FCSTD DOCUMENT  (FreeCAD 0.21R33771 (Git))
Label: RING0_clean
License: All rights reserved
LicenseURL: http://en.wikipedia.org/wiki/All_rights_reserved
objects: Part::Part2DObjectPython×336, App::FeaturePython×48, App::DocumentObjectGroup×2
note: 336 computed .brp shape members not serialized (recipe doc carries the construction recipe); baked Part::Feature solids carry a one-line shape summary decoded from their .brp

FEATURE [Part::Part2DObjectPython] Rectangle  # Draft 2D object (typed FeaturePython)
  Area = 0
  ChamferSize = 0
  Columns = 1
  FilletRadius = 0
  Height = 6
  Length = 6
  MakeFace = false
  Placement = pos=(269.11,-49.15,0) rot=(0,0,1;0rad)
  Rows = 1
FEATURE [App::FeaturePython] Text  # WARN: FeaturePython — macro-defined, semantics opaque (R4)
  Placement = pos=(270.79,-53.3517,0) rot=(0,0,-1;4.73892rad)
  Text = 0
FEATURE [App::FeaturePython] Text001  # WARN: FeaturePython — macro-defined, semantics opaque (R4)
  Placement = pos=(268.047,49.5386,0) rot=(0,0,1;2.6241rad)
  Text = 6.
FEATURE [Part::Part2DObjectPython] Circle  # Draft 2D object (typed FeaturePython)
  Area = 1.13097
  FirstAngle = 0
  LastAngle = 0
  MakeFace = true
  Placement = pos=(275.71,-46.15,0) rot=(0,0,1;0rad)
  Radius = 0.6
FEATURE [Part::Part2DObjectPython] Rectangle001  # Draft 2D object (typed FeaturePython)
  Area = 0
  ChamferSize = 0
  Columns = 1
  FilletRadius = 0
  Height = 6
  Length = 6
  MakeFace = false
  Placement = pos=(271.27,-33.85,0) rot=(0,0,1;0rad)
  Rows = 1
FEATURE [Part::Part2DObjectPython] Circle001  # Draft 2D object (typed FeaturePython)
  Area = 1.13097
  FirstAngle = 0
  LastAngle = 0
  MakeFace = true
  Placement = pos=(277.87,-30.85,0) rot=(0,0,1;0rad)
  Radius = 0.6
FEATURE [Part::Part2DObjectPython] Rectangle002  # Draft 2D object (typed FeaturePython)
  Area = 0
  ChamferSize = 0
  Columns = 1
  FilletRadius = 0
  Height = 6
  Length = 6
  MakeFace = false
  Placement = pos=(279.554,-16.9094,0) rot=(0,0,1;2.00503rad)
  Rows = 1
FEATURE [Part::Part2DObjectPython] Circle002  # Draft 2D object (typed FeaturePython)
  Area = 1.13097
  FirstAngle = 0
  LastAngle = 0
  MakeFace = true
  Placement = pos=(274.055,-12.1841,0) rot=(0,0,1;2.00503rad)
  Radius = 0.6
FEATURE [Part::Part2DObjectPython] Rectangle003  # Draft 2D object (typed FeaturePython)
  Area = 0
  ChamferSize = 0
  Columns = 1
  FilletRadius = 0
  Height = 6
  Length = 6
  MakeFace = false
  Placement = pos=(279.954,-1.537,0) rot=(0,0,1;1.98549rad)
  Rows = 1
FEATURE [Part::Part2DObjectPython] Circle003  # Draft 2D object (typed FeaturePython)
  Area = 1.13097
  FirstAngle = 0
  LastAngle = 0
  MakeFace = true
  Placement = pos=(274.55,3.29487,0) rot=(0,0,1;1.98549rad)
  Radius = 0.6
FEATURE [Part::Part2DObjectPython] Rectangle004  # Draft 2D object (typed FeaturePython)
  Area = 0
  ChamferSize = 0
  Columns = 1
  FilletRadius = 0
  Height = 6
  Length = 6
  MakeFace = false
  Placement = pos=(279.425,13.6792,0) rot=(0,0,1;1.92562rad)
  Rows = 1
FEATURE [Part::Part2DObjectPython] Circle004  # Draft 2D object (typed FeaturePython)
  Area = 1.13097
  FirstAngle = 0
  LastAngle = 0
  MakeFace = true
  Placement = pos=(274.319,18.8257,0) rot=(0,0,1;1.92562rad)
  Radius = 0.6
FEATURE [Part::Part2DObjectPython] Rectangle005  # Draft 2D object (typed FeaturePython)
  Area = 0
  ChamferSize = 0
  Columns = 1
  FilletRadius = 0
  Height = 6
  Length = 6
  MakeFace = false
  Placement = pos=(277.955,28.7473,0) rot=(0,0,1;1.83766rad)
  Rows = 1
FEATURE [Part::Part2DObjectPython] Circle005  # Draft 2D object (typed FeaturePython)
  Area = 1.13097
  FirstAngle = 0
  LastAngle = 0
  MakeFace = true
  Placement = pos=(273.321,34.3226,0) rot=(0,0,1;1.83766rad)
  Radius = 0.6
FEATURE [Part::Part2DObjectPython] Rectangle006  # Draft 2D object (typed FeaturePython)
  Area = 0
  ChamferSize = 0
  Columns = 1
  FilletRadius = 0
  Height = 6
  Length = 6
  MakeFace = false
  Placement = pos=(275.609,43.7506,0) rot=(0,0,1;1.7551rad)
  Rows = 1
FEATURE [Part::Part2DObjectPython] Circle006  # Draft 2D object (typed FeaturePython)
  Area = 1.13097
  FirstAngle = 0
  LastAngle = 0
  MakeFace = true
  Placement = pos=(271.45,49.689,0) rot=(0,0,1;1.7551rad)
  Radius = 0.6
FEATURE [Part::Part2DObjectPython] Rectangle007  # Draft 2D object (typed FeaturePython)
  Area = 0
  ChamferSize = 0
  Columns = 1
  FilletRadius = 0
  Height = 6
  Length = 6
  MakeFace = false
  Placement = pos=(262.426,94.0073,0) rot=(0,0,1;1.84307rad)
  Rows = 1
FEATURE [App::FeaturePython] Text002  # WARN: FeaturePython — macro-defined, semantics opaque (R4)
  Placement = pos=(261.188,89.1931,0) rot=(0,0,-1;4.21532rad)
  Text = 0
FEATURE [App::FeaturePython] Text003  # WARN: FeaturePython — macro-defined, semantics opaque (R4)
  Placement = pos=(207.363,176.926,0) rot=(0,0,1;3.1477rad)
  Text = 7
FEATURE [Part::Part2DObjectPython] Circle007  # Draft 2D object (typed FeaturePython)
  Area = 1.13097
  FirstAngle = 0
  LastAngle = 0
  MakeFace = true
  Placement = pos=(257.762,99.5574,0) rot=(0,0,1;1.84307rad)
  Radius = 0.6
FEATURE [Part::Part2DObjectPython] Rectangle008  # Draft 2D object (typed FeaturePython)
  Area = 0
  ChamferSize = 0
  Columns = 1
  FilletRadius = 0
  Height = 6
  Length = 6
  MakeFace = false
  Placement = pos=(257.005,109.172,0) rot=(0,0,1;2.05774rad)
  Rows = 1
FEATURE [Part::Part2DObjectPython] Circle008  # Draft 2D object (typed FeaturePython)
  Area = 1.13097
  FirstAngle = 0
  LastAngle = 0
  MakeFace = true
  Placement = pos=(251.265,113.602,0) rot=(0,0,1;2.05774rad)
  Radius = 0.6
FEATURE [Part::Part2DObjectPython] Rectangle009  # Draft 2D object (typed FeaturePython)
  Area = 0
  ChamferSize = 0
  Columns = 1
  FilletRadius = 0
  Height = 6
  Length = 6
  MakeFace = false
  Placement = pos=(250.401,125.732,0) rot=(0,0,1;2.67315rad)
  Rows = 1
FEATURE [Part::Part2DObjectPython] Circle009  # Draft 2D object (typed FeaturePython)
  Area = 1.13097
  FirstAngle = 0
  LastAngle = 0
  MakeFace = true
  Placement = pos=(243.158,126.035,0) rot=(0,0,1;2.67315rad)
  Radius = 0.6
FEATURE [Part::Part2DObjectPython] Rectangle010  # Draft 2D object (typed FeaturePython)
  Area = 0
  ChamferSize = 0
  Columns = 1
  FilletRadius = 0
  Height = 6
  Length = 6
  MakeFace = false
  Placement = pos=(237.816,142.068,0) rot=(0,0,-1;2.06856rad)
  Rows = 1
FEATURE [Part::Part2DObjectPython] Circle010  # Draft 2D object (typed FeaturePython)
  Area = 1.13097
  FirstAngle = 0
  LastAngle = 0
  MakeFace = true
  Placement = pos=(237.301,134.837,0) rot=(0,0,-1;2.06856rad)
  Radius = 0.6
FEATURE [Part::Part2DObjectPython] Rectangle011  # Draft 2D object (typed FeaturePython)
  Area = 0
  ChamferSize = 0
  Columns = 1
  FilletRadius = 0
  Height = 6
  Length = 6
  MakeFace = false
  Placement = pos=(227.695,153.917,0) rot=(0,0,-1;1.49278rad)
  Rows = 1
FEATURE [Part::Part2DObjectPython] Circle011  # Draft 2D object (typed FeaturePython)
  Area = 1.13097
  FirstAngle = 0
  LastAngle = 0
  MakeFace = true
  Placement = pos=(231.201,147.571,0) rot=(0,0,-1;1.49278rad)
  Radius = 0.6
FEATURE [Part::Part2DObjectPython] Rectangle012  # Draft 2D object (typed FeaturePython)
  Area = 0
  ChamferSize = 0
  Columns = 1
  FilletRadius = 0
  Height = 6
  Length = 6
  MakeFace = false
  Placement = pos=(218.268,165.67,0) rot=(0,0,-1;1.22889rad)
  Rows = 1
FEATURE [Part::Part2DObjectPython] Circle012  # Draft 2D object (typed FeaturePython)
  Area = 1.13097
  FirstAngle = 0
  LastAngle = 0
  MakeFace = true
  Placement = pos=(223.307,160.458,0) rot=(0,0,-1;1.22889rad)
  Radius = 0.6
FEATURE [Part::Part2DObjectPython] Rectangle013  # Draft 2D object (typed FeaturePython)
  Area = 0
  ChamferSize = 0
  Columns = 1
  FilletRadius = 0
  Height = 6
  Length = 6
  MakeFace = false
  Placement = pos=(208.466,177.056,0) rot=(0,0,-1;1.03219rad)
  Rows = 1
FEATURE [Part::Part2DObjectPython] Circle013  # Draft 2D object (typed FeaturePython)
  Area = 1.13097
  FirstAngle = 0
  LastAngle = 0
  MakeFace = true
  Placement = pos=(214.427,172.93,0) rot=(0,0,-1;1.03219rad)
  Radius = 0.6
FEATURE [Part::Part2DObjectPython] Rectangle014  # Draft 2D object (typed FeaturePython)
  Area = 0
  ChamferSize = 0
  Columns = 1
  FilletRadius = 0
  Height = 6
  Length = 6
  MakeFace = false
  Placement = pos=(171.985,211.268,0) rot=(0,0,-1;0.47089rad)
  Rows = 1
FEATURE [App::FeaturePython] Text004  # WARN: FeaturePython — macro-defined, semantics opaque (R4)
  Placement = pos=(181.597,207.836,0) rot=(0,0,-1;3.69172rad)
  Text = 0
FEATURE [App::FeaturePython] Text005  # WARN: FeaturePython — macro-defined, semantics opaque (R4)
  Placement = pos=(91.1209,256.902,0) rot=(0,0,1;3.6713rad)
  Text = 8
FEATURE [Part::Part2DObjectPython] Circle014  # Draft 2D object (typed FeaturePython)
  Area = 1.13097
  FirstAngle = 0
  LastAngle = 0
  MakeFace = true
  Placement = pos=(179.228,210.947,0) rot=(0,0,-1;0.47089rad)
  Radius = 0.6
FEATURE [Part::Part2DObjectPython] Rectangle015  # Draft 2D object (typed FeaturePython)
  Area = 0
  ChamferSize = 0
  Columns = 1
  FilletRadius = 0
  Height = 6
  Length = 6
  MakeFace = false
  Placement = pos=(160.075,220.163,0) rot=(0,0,-1;0.311367rad)
  Rows = 1
FEATURE [Part::Part2DObjectPython] Circle015  # Draft 2D object (typed FeaturePython)
  Area = 1.13097
  FirstAngle = 0
  LastAngle = 0
  MakeFace = true
  Placement = pos=(167.277,220.997,0) rot=(0,0,-1;0.311367rad)
  Radius = 0.6
FEATURE [Part::Part2DObjectPython] Rectangle016  # Draft 2D object (typed FeaturePython)
  Area = 0
  ChamferSize = 0
  Columns = 1
  FilletRadius = 0
  Height = 6
  Length = 6
  MakeFace = false
  Placement = pos=(147.739,228.41,0) rot=(0,0,-1;0.152367rad)
  Rows = 1
FEATURE [Part::Part2DObjectPython] Circle016  # Draft 2D object (typed FeaturePython)
  Area = 1.13097
  FirstAngle = 0
  LastAngle = 0
  MakeFace = true
  Placement = pos=(154.718,230.374,0) rot=(0,0,-1;0.152367rad)
  Radius = 0.6
FEATURE [Part::Part2DObjectPython] Rectangle017  # Draft 2D object (typed FeaturePython)
  Area = 0
  ChamferSize = 0
  Columns = 1
  FilletRadius = 0
  Height = 6
  Length = 6
  MakeFace = false
  Placement = pos=(134.999,236.021,0) rot=(0,0,-1;0.000349rad)
  Rows = 1
FEATURE [Part::Part2DObjectPython] Circle017  # Draft 2D object (typed FeaturePython)
  Area = 1.13097
  FirstAngle = 0
  LastAngle = 0
  MakeFace = true
  Placement = pos=(141.6,239.019,0) rot=(0,0,-1;0.000349rad)
  Radius = 0.6
FEATURE [Part::Part2DObjectPython] Rectangle018  # Draft 2D object (typed FeaturePython)
  Area = 0
  ChamferSize = 0
  Columns = 1
  FilletRadius = 0
  Height = 6
  Length = 6
  MakeFace = false
  Placement = pos=(121.98,242.893,0) rot=(0,0,1;0.175406rad)
  Rows = 1
FEATURE [Part::Part2DObjectPython] Circle018  # Draft 2D object (typed FeaturePython)
  Area = 1.13097
  FirstAngle = 0
  LastAngle = 0
  MakeFace = true
  Placement = pos=(127.955,246.998,0) rot=(0,0,1;0.175406rad)
  Radius = 0.6
FEATURE [Part::Part2DObjectPython] Rectangle019  # Draft 2D object (typed FeaturePython)
  Area = 0
  ChamferSize = 0
  Columns = 1
  FilletRadius = 0
  Height = 6
  Length = 6
  MakeFace = false
  Placement = pos=(107.42,249.95,0) rot=(0,0,1;0rad)
  Rows = 1
FEATURE [Part::Part2DObjectPython] Circle019  # Draft 2D object (typed FeaturePython)
  Area = 1.13097
  FirstAngle = 0
  LastAngle = 0
  MakeFace = true
  Placement = pos=(114.02,252.95,0) rot=(0,0,1;0rad)
  Radius = 0.6
FEATURE [Part::Part2DObjectPython] Rectangle020  # Draft 2D object (typed FeaturePython)
  Area = 0
  ChamferSize = 0
  Columns = 1
  FilletRadius = 0
  Height = 6
  Length = 6
  MakeFace = false
  Placement = pos=(93.09,255.73,0) rot=(0,0,1;0rad)
  Rows = 1
FEATURE [Part::Part2DObjectPython] Circle020  # Draft 2D object (typed FeaturePython)
  Area = 1.13097
  FirstAngle = 0
  LastAngle = 0
  MakeFace = true
  Placement = pos=(99.69,258.73,0) rot=(0,0,1;0rad)
  Radius = 0.6
FEATURE [Part::Part2DObjectPython] Rectangle021  # Draft 2D object (typed FeaturePython)
  Area = 0
  ChamferSize = 0
  Columns = 1
  FilletRadius = 0
  Height = 6
  Length = 6
  MakeFace = false
  Placement = pos=(43.15,269.11,0) rot=(0,0,1;0rad)
  Rows = 1
FEATURE [App::FeaturePython] Text006  # WARN: FeaturePython — macro-defined, semantics opaque (R4)
  Placement = pos=(53.3517,270.79,0) rot=(0,0,-1;3.16812rad)
  Text = 0
FEATURE [App::FeaturePython] Text007  # WARN: FeaturePython — macro-defined, semantics opaque (R4)
  Placement = pos=(-49.5386,268.047,0) rot=(0,0,1;4.1949rad)
  Text = 9
FEATURE [Part::Part2DObjectPython] Circle021  # Draft 2D object (typed FeaturePython)
  Area = 1.13097
  FirstAngle = 0
  LastAngle = 0
  MakeFace = true
  Placement = pos=(49.75,272.11,0) rot=(0,0,1;0rad)
  Radius = 0.6
FEATURE [Part::Part2DObjectPython] Rectangle022  # Draft 2D object (typed FeaturePython)
  Area = 0
  ChamferSize = 0
  Columns = 1
  FilletRadius = 0
  Height = 6
  Length = 6
  MakeFace = false
  Placement = pos=(27.85,271.27,0) rot=(0,0,1;0rad)
  Rows = 1
FEATURE [Part::Part2DObjectPython] Circle022  # Draft 2D object (typed FeaturePython)
  Area = 1.13097
  FirstAngle = 0
  LastAngle = 0
  MakeFace = true
  Placement = pos=(34.45,274.27,0) rot=(0,0,1;0rad)
  Radius = 0.6
FEATURE [Part::Part2DObjectPython] Rectangle023  # Draft 2D object (typed FeaturePython)
  Area = 0
  ChamferSize = 0
  Columns = 1
  FilletRadius = 0
  Height = 6
  Length = 6
  MakeFace = false
  Placement = pos=(12.45,272.57,0) rot=(0,0,1;0rad)
  Rows = 1
FEATURE [Part::Part2DObjectPython] Circle023  # Draft 2D object (typed FeaturePython)
  Area = 1.13097
  FirstAngle = 0
  LastAngle = 0
  MakeFace = true
  Placement = pos=(19.05,275.57,0) rot=(0,0,1;0rad)
  Radius = 0.6
FEATURE [Part::Part2DObjectPython] Rectangle024  # Draft 2D object (typed FeaturePython)
  Area = 0
  ChamferSize = 0
  Columns = 1
  FilletRadius = 0
  Height = 6
  Length = 6
  MakeFace = false
  Placement = pos=(-3,273,0) rot=(0,0,1;0rad)
  Rows = 1
FEATURE [Part::Part2DObjectPython] Circle024  # Draft 2D object (typed FeaturePython)
  Area = 1.13097
  FirstAngle = 0
  LastAngle = 0
  MakeFace = true
  Placement = pos=(3.6,276,0) rot=(0,0,1;0rad)
  Radius = 0.6
FEATURE [Part::Part2DObjectPython] Rectangle025  # Draft 2D object (typed FeaturePython)
  Area = 0
  ChamferSize = 0
  Columns = 1
  FilletRadius = 0
  Height = 6
  Length = 6
  MakeFace = false
  Placement = pos=(-11.2074,275.547,0) rot=(0,0,1;2.35078rad)
  Rows = 1
FEATURE [Part::Part2DObjectPython] Circle025  # Draft 2D object (typed FeaturePython)
  Area = 1.13097
  FirstAngle = 0
  LastAngle = 0
  MakeFace = true
  Placement = pos=(-17.9818,278.129,0) rot=(0,0,1;2.35078rad)
  Radius = 0.6
FEATURE [Part::Part2DObjectPython] Rectangle026  # Draft 2D object (typed FeaturePython)
  Area = 0
  ChamferSize = 0
  Columns = 1
  FilletRadius = 0
  Height = 6
  Length = 6
  MakeFace = false
  Placement = pos=(-26.6143,274.513,0) rot=(0,0,1;2.41344rad)
  Rows = 1
FEATURE [Part::Part2DObjectPython] Circle026  # Draft 2D object (typed FeaturePython)
  Area = 1.13097
  FirstAngle = 0
  LastAngle = 0
  MakeFace = true
  Placement = pos=(-33.5371,276.666,0) rot=(0,0,1;2.41344rad)
  Radius = 0.6
FEATURE [Part::Part2DObjectPython] Rectangle027  # Draft 2D object (typed FeaturePython)
  Area = 0
  ChamferSize = 0
  Columns = 1
  FilletRadius = 0
  Height = 6
  Length = 6
  MakeFace = false
  Placement = pos=(-41.9327,272.573,0) rot=(0,0,1;2.46545rad)
  Rows = 1
FEATURE [Part::Part2DObjectPython] Circle027  # Draft 2D object (typed FeaturePython)
  Area = 1.13097
  FirstAngle = 0
  LastAngle = 0
  MakeFace = true
  Placement = pos=(-48.958,274.363,0) rot=(0,0,1;2.46545rad)
  Radius = 0.6
FEATURE [Part::Part2DObjectPython] Rectangle028  # Draft 2D object (typed FeaturePython)
  Area = 0
  ChamferSize = 0
  Columns = 1
  FilletRadius = 0
  Height = 6
  Length = 6
  MakeFace = false
  Placement = pos=(-92.1068,260.191,0) rot=(0,0,1;2.7077rad)
  Rows = 1
FEATURE [App::FeaturePython] Text008  # WARN: FeaturePython — macro-defined, semantics opaque (R4)
  Placement = pos=(-89.1931,261.188,0) rot=(0,0,-1;2.64452rad)
  Text = 0
FEATURE [App::FeaturePython] Text009  # WARN: FeaturePython — macro-defined, semantics opaque (R4)
  Placement = pos=(-176.926,207.363,0) rot=(0,0,1;4.7185rad)
  Text = 10
FEATURE [Part::Part2DObjectPython] Circle028  # Draft 2D object (typed FeaturePython)
  Area = 1.13097
  FirstAngle = 0
  LastAngle = 0
  MakeFace = true
  Placement = pos=(-99.3564,260.243,0) rot=(0,0,1;2.7077rad)
  Radius = 0.6
FEATURE [Part::Part2DObjectPython] Rectangle029  # Draft 2D object (typed FeaturePython)
  Area = 0
  ChamferSize = 0
  Columns = 1
  FilletRadius = 0
  Height = 6
  Length = 6
  MakeFace = false
  Placement = pos=(-106.607,254.81,0) rot=(0,0,1;2.80998rad)
  Rows = 1
FEATURE [Part::Part2DObjectPython] Circle029  # Draft 2D object (typed FeaturePython)
  Area = 1.13097
  FirstAngle = 0
  LastAngle = 0
  MakeFace = true
  Placement = pos=(-113.824,254.122,0) rot=(0,0,1;2.80998rad)
  Radius = 0.6
FEATURE [Part::Part2DObjectPython] Rectangle030  # Draft 2D object (typed FeaturePython)
  Area = 0
  ChamferSize = 0
  Columns = 1
  FilletRadius = 0
  Height = 6
  Length = 6
  MakeFace = false
  Placement = pos=(-120.843,248.666,0) rot=(0,0,1;2.92814rad)
  Rows = 1
FEATURE [Part::Part2DObjectPython] Circle030  # Draft 2D object (typed FeaturePython)
  Area = 1.13097
  FirstAngle = 0
  LastAngle = 0
  MakeFace = true
  Placement = pos=(-127.928,247.133,0) rot=(0,0,1;2.92814rad)
  Radius = 0.6
FEATURE [Part::Part2DObjectPython] Rectangle031  # Draft 2D object (typed FeaturePython)
  Area = 0
  ChamferSize = 0
  Columns = 1
  FilletRadius = 0
  Height = 6
  Length = 6
  MakeFace = false
  Placement = pos=(-134.775,241.777,0) rot=(0,0,1;3.06358rad)
  Rows = 1
FEATURE [Part::Part2DObjectPython] Circle031  # Draft 2D object (typed FeaturePython)
  Area = 1.13097
  FirstAngle = 0
  LastAngle = 0
  MakeFace = true
  Placement = pos=(-141.589,239.301,0) rot=(0,0,1;3.06358rad)
  Radius = 0.6
FEATURE [Part::Part2DObjectPython] Rectangle032  # Draft 2D object (typed FeaturePython)
  Area = 0
  ChamferSize = 0
  Columns = 1
  FilletRadius = 0
  Height = 6
  Length = 6
  MakeFace = false
  Placement = pos=(-148.392,234.135,0) rot=(0,0,1;3.21612rad)
  Rows = 1
FEATURE [Part::Part2DObjectPython] Circle032  # Draft 2D object (typed FeaturePython)
  Area = 1.13097
  FirstAngle = 0
  LastAngle = 0
  MakeFace = true
  Placement = pos=(-154.75,230.652,0) rot=(0,0,1;3.21612rad)
  Radius = 0.6
FEATURE [Part::Part2DObjectPython] Rectangle033  # Draft 2D object (typed FeaturePython)
  Area = 0
  ChamferSize = 0
  Columns = 1
  FilletRadius = 0
  Height = 6
  Length = 6
  MakeFace = false
  Placement = pos=(-161.674,225.742,0) rot=(0,0,1;3.38838rad)
  Rows = 1
FEATURE [Part::Part2DObjectPython] Circle033  # Draft 2D object (typed FeaturePython)
  Area = 1.13097
  FirstAngle = 0
  LastAngle = 0
  MakeFace = true
  Placement = pos=(-167.341,221.221,0) rot=(0,0,1;3.38838rad)
  Radius = 0.6
FEATURE [Part::Part2DObjectPython] Rectangle034  # Draft 2D object (typed FeaturePython)
  Area = 0
  ChamferSize = 0
  Columns = 1
  FilletRadius = 0
  Height = 6
  Length = 6
  MakeFace = false
  Placement = pos=(-174.591,216.575,0) rot=(0,0,1;3.58351rad)
  Rows = 1
FEATURE [Part::Part2DObjectPython] Circle034  # Draft 2D object (typed FeaturePython)
  Area = 1.13097
  FirstAngle = 0
  LastAngle = 0
  MakeFace = true
  Placement = pos=(-179.274,211.04,0) rot=(0,0,1;3.58351rad)
  Radius = 0.6
FEATURE [Part::Part2DObjectPython] Rectangle035  # Draft 2D object (typed FeaturePython)
  Area = 0
  ChamferSize = 0
  Columns = 1
  FilletRadius = 0
  Height = 6
  Length = 6
  MakeFace = false
  Placement = pos=(-215.58,173.02,0) rot=(0,0,1;0rad)
  Rows = 1
FEATURE [App::FeaturePython] Text010  # WARN: FeaturePython — macro-defined, semantics opaque (R4)
  Placement = pos=(-207.836,181.597,0) rot=(0,0,-1;2.12092rad)
  Text = 0
FEATURE [App::FeaturePython] Text011  # WARN: FeaturePython — macro-defined, semantics opaque (R4)
  Placement = pos=(-256.902,91.1209,0) rot=(0,0,1;5.2421rad)
  Text = 11
FEATURE [Part::Part2DObjectPython] Circle035  # Draft 2D object (typed FeaturePython)
  Area = 1.13097
  FirstAngle = 0
  LastAngle = 0
  MakeFace = true
  Placement = pos=(-208.98,176.02,0) rot=(0,0,1;0rad)
  Radius = 0.6
FEATURE [Part::Part2DObjectPython] Rectangle036  # Draft 2D object (typed FeaturePython)
  Area = 0
  ChamferSize = 0
  Columns = 1
  FilletRadius = 0
  Height = 6
  Length = 6
  MakeFace = false
  Placement = pos=(-225.1,160.85,0) rot=(0,0,1;0rad)
  Rows = 1
FEATURE [Part::Part2DObjectPython] Circle036  # Draft 2D object (typed FeaturePython)
  Area = 1.13097
  FirstAngle = 0
  LastAngle = 0
  MakeFace = true
  Placement = pos=(-218.5,163.85,0) rot=(0,0,1;0rad)
  Radius = 0.6
FEATURE [Part::Part2DObjectPython] Rectangle037  # Draft 2D object (typed FeaturePython)
  Area = 0
  ChamferSize = 0
  Columns = 1
  FilletRadius = 0
  Height = 6
  Length = 6
  MakeFace = false
  Placement = pos=(-235.027,152.225,0) rot=(0,0,-1;1.03917rad)
  Rows = 1
FEATURE [Part::Part2DObjectPython] Circle037  # Draft 2D object (typed FeaturePython)
  Area = 1.13097
  FirstAngle = 0
  LastAngle = 0
  MakeFace = true
  Placement = pos=(-229.095,148.057,0) rot=(0,0,-1;1.03917rad)
  Radius = 0.6
FEATURE [Part::Part2DObjectPython] Rectangle038  # Draft 2D object (typed FeaturePython)
  Area = 0
  ChamferSize = 0
  Columns = 1
  FilletRadius = 0
  Height = 6
  Length = 6
  MakeFace = false
  Placement = pos=(-243.205,137.304,0) rot=(0,0,-1;0.620639rad)
  Rows = 1
FEATURE [Part::Part2DObjectPython] Circle038  # Draft 2D object (typed FeaturePython)
  Area = 1.13097
  FirstAngle = 0
  LastAngle = 0
  MakeFace = true
  Placement = pos=(-236.091,135.906,0) rot=(0,0,-1;0.620639rad)
  Radius = 0.6
FEATURE [Part::Part2DObjectPython] Rectangle039  # Draft 2D object (typed FeaturePython)
  Area = 0
  ChamferSize = 0
  Columns = 1
  FilletRadius = 0
  Height = 6
  Length = 6
  MakeFace = false
  Placement = pos=(-249.949,122.131,0) rot=(0,0,-1;0.218341rad)
  Rows = 1
FEATURE [Part::Part2DObjectPython] Circle039  # Draft 2D object (typed FeaturePython)
  Area = 1.13097
  FirstAngle = 0
  LastAngle = 0
  MakeFace = true
  Placement = pos=(-242.855,123.63,0) rot=(0,0,-1;0.218341rad)
  Radius = 0.6
FEATURE [Part::Part2DObjectPython] Rectangle040  # Draft 2D object (typed FeaturePython)
  Area = 0
  ChamferSize = 0
  Columns = 1
  FilletRadius = 0
  Height = 6
  Length = 6
  MakeFace = false
  Placement = pos=(-255.95,107.42,0) rot=(0,0,1;0rad)
  Rows = 1
FEATURE [Part::Part2DObjectPython] Circle040  # Draft 2D object (typed FeaturePython)
  Area = 1.13097
  FirstAngle = 0
  LastAngle = 0
  MakeFace = true
  Placement = pos=(-249.35,110.42,0) rot=(0,0,1;0rad)
  Radius = 0.6
FEATURE [Part::Part2DObjectPython] Rectangle041  # Draft 2D object (typed FeaturePython)
  Area = 0
  ChamferSize = 0
  Columns = 1
  FilletRadius = 0
  Height = 6
  Length = 6
  MakeFace = false
  Placement = pos=(-261.73,93.09,0) rot=(0,0,1;0rad)
  Rows = 1
FEATURE [Part::Part2DObjectPython] Circle041  # Draft 2D object (typed FeaturePython)
  Area = 1.13097
  FirstAngle = 0
  LastAngle = 0
  MakeFace = true
  Placement = pos=(-255.13,96.09,0) rot=(0,0,1;0rad)
  Radius = 0.6
FEATURE [Part::Part2DObjectPython] Rectangle042  # Draft 2D object (typed FeaturePython)
  Area = 0
  ChamferSize = 0
  Columns = 1
  FilletRadius = 0
  Height = 6
  Length = 6
  MakeFace = false
  Placement = pos=(-275.11,43.15,0) rot=(0,0,1;0rad)
  Rows = 1
FEATURE [App::FeaturePython] Text012  # WARN: FeaturePython — macro-defined, semantics opaque (R4)
  Placement = pos=(-270.79,53.3517,0) rot=(0,0,-1;1.59733rad)
  Text = 0
FEATURE [App::FeaturePython] Text013  # WARN: FeaturePython — macro-defined, semantics opaque (R4)
  Placement = pos=(-268.047,-49.5386,0) rot=(0,0,1;5.7657rad)
  Text = 12
FEATURE [Part::Part2DObjectPython] Circle042  # Draft 2D object (typed FeaturePython)
  Area = 1.13097
  FirstAngle = 0
  LastAngle = 0
  MakeFace = true
  Placement = pos=(-268.51,46.15,0) rot=(0,0,1;0rad)
  Radius = 0.6
FEATURE [Part::Part2DObjectPython] Rectangle043  # Draft 2D object (typed FeaturePython)
  Area = 0
  ChamferSize = 0
  Columns = 1
  FilletRadius = 0
  Height = 6
  Length = 6
  MakeFace = false
  Placement = pos=(-277.27,27.85,0) rot=(0,0,1;0rad)
  Rows = 1
FEATURE [Part::Part2DObjectPython] Circle043  # Draft 2D object (typed FeaturePython)
  Area = 1.13097
  FirstAngle = 0
  LastAngle = 0
  MakeFace = true
  Placement = pos=(-270.67,30.85,0) rot=(0,0,1;0rad)
  Radius = 0.6
FEATURE [Part::Part2DObjectPython] Rectangle044  # Draft 2D object (typed FeaturePython)
  Area = 0
  ChamferSize = 0
  Columns = 1
  FilletRadius = 0
  Height = 6
  Length = 6
  MakeFace = false
  Placement = pos=(-278.57,12.45,0) rot=(0,0,1;0rad)
  Rows = 1
FEATURE [Part::Part2DObjectPython] Circle044  # Draft 2D object (typed FeaturePython)
  Area = 1.13097
  FirstAngle = 0
  LastAngle = 0
  MakeFace = true
  Placement = pos=(-271.97,15.45,0) rot=(0,0,1;0rad)
  Radius = 0.6
FEATURE [Part::Part2DObjectPython] Rectangle045  # Draft 2D object (typed FeaturePython)
  Area = 0
  ChamferSize = 0
  Columns = 1
  FilletRadius = 0
  Height = 6
  Length = 6
  MakeFace = false
  Placement = pos=(-272.368,-2.19273,0) rot=(0,0,1;1.81305rad)
  Rows = 1
FEATURE [Part::Part2DObjectPython] Circle045  # Draft 2D object (typed FeaturePython)
  Area = 1.13097
  FirstAngle = 0
  LastAngle = 0
  MakeFace = true
  Placement = pos=(-276.864,3.49488,0) rot=(0,0,1;1.81305rad)
  Radius = 0.6
FEATURE [Part::Part2DObjectPython] Rectangle046  # Draft 2D object (typed FeaturePython)
  Area = 0
  ChamferSize = 0
  Columns = 1
  FilletRadius = 0
  Height = 6
  Length = 6
  MakeFace = false
  Placement = pos=(-271.699,-17.1865,0) rot=(0,0,1;1.93452rad)
  Rows = 1
FEATURE [Part::Part2DObjectPython] Circle046  # Draft 2D object (typed FeaturePython)
  Area = 1.13097
  FirstAngle = 0
  LastAngle = 0
  MakeFace = true
  Placement = pos=(-276.851,-12.0855,0) rot=(0,0,1;1.93452rad)
  Radius = 0.6
FEATURE [Part::Part2DObjectPython] Rectangle047  # Draft 2D object (typed FeaturePython)
  Area = 0
  ChamferSize = 0
  Columns = 1
  FilletRadius = 0
  Height = 6
  Length = 6
  MakeFace = false
  Placement = pos=(-270.258,-32.2306,0) rot=(0,0,1;2.02476rad)
  Rows = 1
FEATURE [Part::Part2DObjectPython] Circle047  # Draft 2D object (typed FeaturePython)
  Area = 1.13097
  FirstAngle = 0
  LastAngle = 0
  MakeFace = true
  Placement = pos=(-275.849,-27.6146,0) rot=(0,0,1;2.02476rad)
  Radius = 0.6
FEATURE [Part::Part2DObjectPython] Rectangle048  # Draft 2D object (typed FeaturePython)
  Area = 0
  ChamferSize = 0
  Columns = 1
  FilletRadius = 0
  Height = 6
  Length = 6
  MakeFace = false
  Placement = pos=(-268.022,-47.2859,0) rot=(0,0,1;2.08514rad)
  Rows = 1
FEATURE [Part::Part2DObjectPython] Circle048  # Draft 2D object (typed FeaturePython)
  Area = 1.13097
  FirstAngle = 0
  LastAngle = 0
  MakeFace = true
  Placement = pos=(-273.881,-43.0158,0) rot=(0,0,1;2.08514rad)
  Radius = 0.6
FEATURE [Part::Part2DObjectPython] Rectangle049  # Draft 2D object (typed FeaturePython)
  Area = 0
  ChamferSize = 0
  Columns = 1
  FilletRadius = 0
  Height = 6
  Length = 6
  MakeFace = false
  Placement = pos=(-254.646,-97.2388,0) rot=(0,0,1;2.082rad)
  Rows = 1
FEATURE [App::FeaturePython] Text014  # WARN: FeaturePython — macro-defined, semantics opaque (R4)
  Placement = pos=(-261.188,-89.1931,0) rot=(0,0,-1;1.07373rad)
  Text = 0
FEATURE [App::FeaturePython] Text015  # WARN: FeaturePython — macro-defined, semantics opaque (R4)
  Placement = pos=(-207.363,-176.926,0) rot=(0,0,-1;6.27708rad)
  Text = 1
FEATURE [Part::Part2DObjectPython] Circle049  # Draft 2D object (typed FeaturePython)
  Area = 1.13097
  FirstAngle = 0
  LastAngle = 0
  MakeFace = true
  Placement = pos=(-260.491,-92.9502,0) rot=(0,0,1;2.082rad)
  Radius = 0.6
FEATURE [Part::Part2DObjectPython] Rectangle050  # Draft 2D object (typed FeaturePython)
  Area = 0
  ChamferSize = 0
  Columns = 1
  FilletRadius = 0
  Height = 6
  Length = 6
  MakeFace = false
  Placement = pos=(-248.887,-111.641,0) rot=(0,0,1;2.06438rad)
  Rows = 1
FEATURE [Part::Part2DObjectPython] Circle050  # Draft 2D object (typed FeaturePython)
  Area = 1.13097
  FirstAngle = 0
  LastAngle = 0
  MakeFace = true
  Placement = pos=(-254.656,-107.25,0) rot=(0,0,1;2.06438rad)
  Radius = 0.6
FEATURE [Part::Part2DObjectPython] Rectangle051  # Draft 2D object (typed FeaturePython)
  Area = 0
  ChamferSize = 0
  Columns = 1
  FilletRadius = 0
  Height = 6
  Length = 6
  MakeFace = false
  Placement = pos=(-242.318,-125.667,0) rot=(0,0,1;2.05547rad)
  Rows = 1
FEATURE [Part::Part2DObjectPython] Circle051  # Draft 2D object (typed FeaturePython)
  Area = 1.13097
  FirstAngle = 0
  LastAngle = 0
  MakeFace = true
  Placement = pos=(-248.047,-121.225,0) rot=(0,0,1;2.05547rad)
  Radius = 0.6
FEATURE [Part::Part2DObjectPython] Rectangle052  # Draft 2D object (typed FeaturePython)
  Area = 0
  ChamferSize = 0
  Columns = 1
  FilletRadius = 0
  Height = 6
  Length = 6
  MakeFace = false
  Placement = pos=(-235.006,-139.374,0) rot=(0,0,1;2.0265rad)
  Rows = 1
FEATURE [Part::Part2DObjectPython] Circle052  # Draft 2D object (typed FeaturePython)
  Area = 1.13097
  FirstAngle = 0
  LastAngle = 0
  MakeFace = true
  Placement = pos=(-240.604,-134.767,0) rot=(0,0,1;2.0265rad)
  Radius = 0.6
FEATURE [Part::Part2DObjectPython] Rectangle053  # Draft 2D object (typed FeaturePython)
  Area = 0
  ChamferSize = 0
  Columns = 1
  FilletRadius = 0
  Height = 6
  Length = 6
  MakeFace = false
  Placement = pos=(-229.308,-155.084,0) rot=(0,0,1;1.17513rad)
  Rows = 1
FEATURE [Part::Part2DObjectPython] Circle053  # Draft 2D object (typed FeaturePython)
  Area = 1.13097
  FirstAngle = 0
  LastAngle = 0
  MakeFace = true
  Placement = pos=(-229.532,-147.838,0) rot=(0,0,1;1.17513rad)
  Radius = 0.6
FEATURE [Part::Part2DObjectPython] Rectangle054  # Draft 2D object (typed FeaturePython)
  Area = 0
  ChamferSize = 0
  Columns = 1
  FilletRadius = 0
  Height = 6
  Length = 6
  MakeFace = false
  Placement = pos=(-225.094,-166.856,0) rot=(0,0,1;0.00192rad)
  Rows = 1
FEATURE [Part::Part2DObjectPython] Circle054  # Draft 2D object (typed FeaturePython)
  Area = 1.13097
  FirstAngle = 0
  LastAngle = 0
  MakeFace = true
  Placement = pos=(-218.5,-163.843,0) rot=(0,0,1;0.00192rad)
  Radius = 0.6
FEATURE [Part::Part2DObjectPython] Rectangle055  # Draft 2D object (typed FeaturePython)
  Area = 0
  ChamferSize = 0
  Columns = 1
  FilletRadius = 0
  Height = 6
  Length = 6
  MakeFace = false
  Placement = pos=(-215.58,-179.02,0) rot=(0,0,1;0rad)
  Rows = 1
FEATURE [Part::Part2DObjectPython] Circle055  # Draft 2D object (typed FeaturePython)
  Area = 1.13097
  FirstAngle = 0
  LastAngle = 0
  MakeFace = true
  Placement = pos=(-208.98,-176.02,0) rot=(0,0,1;0rad)
  Radius = 0.6
FEATURE [Part::Part2DObjectPython] Rectangle056  # Draft 2D object (typed FeaturePython)
  Area = 0
  ChamferSize = 0
  Columns = 1
  FilletRadius = 0
  Height = 6
  Length = 6
  MakeFace = false
  Placement = pos=(-179.02,-215.58,0) rot=(0,0,1;0rad)
  Rows = 1
FEATURE [App::FeaturePython] Text016  # WARN: FeaturePython — macro-defined, semantics opaque (R4)
  Placement = pos=(-181.597,-207.836,0) rot=(0,0,-1;0.550128rad)
  Text = 0
FEATURE [App::FeaturePython] Text017  # WARN: FeaturePython — macro-defined, semantics opaque (R4)
  Placement = pos=(-91.1209,-256.902,0) rot=(0,0,-1;5.75348rad)
  Text = 2
FEATURE [Part::Part2DObjectPython] Circle056  # Draft 2D object (typed FeaturePython)
  Area = 1.13097
  FirstAngle = 0
  LastAngle = 0
  MakeFace = true
  Placement = pos=(-172.42,-212.58,0) rot=(0,0,1;0rad)
  Radius = 0.6
FEATURE [Part::Part2DObjectPython] Rectangle057  # Draft 2D object (typed FeaturePython)
  Area = 0
  ChamferSize = 0
  Columns = 1
  FilletRadius = 0
  Height = 6
  Length = 6
  MakeFace = false
  Placement = pos=(-166.85,-225.1,0) rot=(0,0,1;0rad)
  Rows = 1
FEATURE [Part::Part2DObjectPython] Circle057  # Draft 2D object (typed FeaturePython)
  Area = 1.13097
  FirstAngle = 0
  LastAngle = 0
  MakeFace = true
  Placement = pos=(-160.25,-222.1,0) rot=(0,0,1;0rad)
  Radius = 0.6
FEATURE [Part::Part2DObjectPython] Rectangle058  # Draft 2D object (typed FeaturePython)
  Area = 0
  ChamferSize = 0
  Columns = 1
  FilletRadius = 0
  Height = 6
  Length = 6
  MakeFace = false
  Placement = pos=(-153.761,-234.272,0) rot=(0,0,1;0.125489rad)
  Rows = 1
FEATURE [Part::Part2DObjectPython] Circle058  # Draft 2D object (typed FeaturePython)
  Area = 1.13097
  FirstAngle = 0
  LastAngle = 0
  MakeFace = true
  Placement = pos=(-147.588,-230.469,0) rot=(0,0,1;0.125489rad)
  Radius = 0.6
FEATURE [Part::Part2DObjectPython] Rectangle059  # Draft 2D object (typed FeaturePython)
  Area = 0
  ChamferSize = 0
  Columns = 1
  FilletRadius = 0
  Height = 6
  Length = 6
  MakeFace = false
  Placement = pos=(-140.093,-242.71,0) rot=(0,0,1;0.269479rad)
  Rows = 1
FEATURE [Part::Part2DObjectPython] Circle059  # Draft 2D object (typed FeaturePython)
  Area = 1.13097
  FirstAngle = 0
  LastAngle = 0
  MakeFace = true
  Placement = pos=(-134.53,-238.062,0) rot=(0,0,1;0.269479rad)
  Radius = 0.6
FEATURE [Part::Part2DObjectPython] Rectangle060  # Draft 2D object (typed FeaturePython)
  Area = 0
  ChamferSize = 0
  Columns = 1
  FilletRadius = 0
  Height = 6
  Length = 6
  MakeFace = false
  Placement = pos=(-125.95,-250.323,0) rot=(0,0,1;0.413818rad)
  Rows = 1
FEATURE [Part::Part2DObjectPython] Circle060  # Draft 2D object (typed FeaturePython)
  Area = 1.13097
  FirstAngle = 0
  LastAngle = 0
  MakeFace = true
  Placement = pos=(-121.114,-244.922,0) rot=(0,0,1;0.413818rad)
  Radius = 0.6
FEATURE [Part::Part2DObjectPython] Rectangle061  # Draft 2D object (typed FeaturePython)
  Area = 0
  ChamferSize = 0
  Columns = 1
  FilletRadius = 0
  Height = 6
  Length = 6
  MakeFace = false
  Placement = pos=(-111.377,-257.083,0) rot=(0,0,1;0.557982rad)
  Rows = 1
FEATURE [Part::Part2DObjectPython] Circle061  # Draft 2D object (typed FeaturePython)
  Area = 1.13097
  FirstAngle = 0
  LastAngle = 0
  MakeFace = true
  Placement = pos=(-107.366,-251.044,0) rot=(0,0,1;0.557982rad)
  Radius = 0.6
FEATURE [Part::Part2DObjectPython] Rectangle062  # Draft 2D object (typed FeaturePython)
  Area = 0
  ChamferSize = 0
  Columns = 1
  FilletRadius = 0
  Height = 6
  Length = 6
  MakeFace = false
  Placement = pos=(-96.445,-262.958,0) rot=(0,0,1;0.701622rad)
  Rows = 1
FEATURE [Part::Part2DObjectPython] Circle062  # Draft 2D object (typed FeaturePython)
  Area = 1.13097
  FirstAngle = 0
  LastAngle = 0
  MakeFace = true
  Placement = pos=(-93.3403,-256.406,0) rot=(0,0,1;0.701622rad)
  Radius = 0.6
FEATURE [Part::Part2DObjectPython] Rectangle063  # Draft 2D object (typed FeaturePython)
  Area = 0
  ChamferSize = 0
  Columns = 1
  FilletRadius = 0
  Height = 6
  Length = 6
  MakeFace = false
  Placement = pos=(-44.495,-276.017,0) rot=(0,0,1;1.18613rad)
  Rows = 1
FEATURE [App::FeaturePython] Text018  # WARN: FeaturePython — macro-defined, semantics opaque (R4)
  Placement = pos=(-53.3517,-270.79,0) rot=(0,0,1;6.25666rad)
  Text = 0
FEATURE [App::FeaturePython] Text019  # WARN: FeaturePython — macro-defined, semantics opaque (R4)
  Placement = pos=(49.5386,-268.047,0) rot=(0,0,1;1.05331rad)
  Text = 3
FEATURE [Part::Part2DObjectPython] Circle063  # Draft 2D object (typed FeaturePython)
  Area = 1.13097
  FirstAngle = 0
  LastAngle = 0
  MakeFace = true
  Placement = pos=(-44.7991,-268.773,0) rot=(0,0,1;1.18613rad)
  Radius = 0.6
FEATURE [Part::Part2DObjectPython] Rectangle064  # Draft 2D object (typed FeaturePython)
  Area = 0
  ChamferSize = 0
  Columns = 1
  FilletRadius = 0
  Height = 6
  Length = 6
  MakeFace = false
  Placement = pos=(-28.6459,-277.895,0) rot=(0,0,1;1.33169rad)
  Rows = 1
FEATURE [Part::Part2DObjectPython] Circle064  # Draft 2D object (typed FeaturePython)
  Area = 1.13097
  FirstAngle = 0
  LastAngle = 0
  MakeFace = true
  Placement = pos=(-29.9974,-270.772,0) rot=(0,0,1;1.33169rad)
  Radius = 0.6
FEATURE [Part::Part2DObjectPython] Rectangle065  # Draft 2D object (typed FeaturePython)
  Area = 0
  ChamferSize = 0
  Columns = 1
  FilletRadius = 0
  Height = 6
  Length = 6
  MakeFace = false
  Placement = pos=(-18.45,-278.57,0) rot=(0,0,1;0rad)
  Rows = 1
FEATURE [Part::Part2DObjectPython] Circle065  # Draft 2D object (typed FeaturePython)
  Area = 1.13097
  FirstAngle = 0
  LastAngle = 0
  MakeFace = true
  Placement = pos=(-11.85,-275.57,0) rot=(0,0,1;0rad)
  Radius = 0.6
FEATURE [Part::Part2DObjectPython] Rectangle066  # Draft 2D object (typed FeaturePython)
  Area = 0
  ChamferSize = 0
  Columns = 1
  FilletRadius = 0
  Height = 6
  Length = 6
  MakeFace = false
  Placement = pos=(3.1687,-278.821,0) rot=(0,0,1;1.62874rad)
  Rows = 1
FEATURE [Part::Part2DObjectPython] Circle066  # Draft 2D object (typed FeaturePython)
  Area = 1.13097
  FirstAngle = 0
  LastAngle = 0
  MakeFace = true
  Placement = pos=(-0.208485,-272.406,0) rot=(0,0,1;1.62874rad)
  Radius = 0.6
FEATURE [Part::Part2DObjectPython] Rectangle067  # Draft 2D object (typed FeaturePython)
  Area = 0
  ChamferSize = 0
  Columns = 1
  FilletRadius = 0
  Height = 6
  Length = 6
  MakeFace = false
  Placement = pos=(19.0033,-277.888,0) rot=(0,0,1;1.77814rad)
  Rows = 1
FEATURE [Part::Part2DObjectPython] Circle067  # Draft 2D object (typed FeaturePython)
  Area = 1.13097
  FirstAngle = 0
  LastAngle = 0
  MakeFace = true
  Placement = pos=(14.7089,-272.047,0) rot=(0,0,1;1.77814rad)
  Radius = 0.6
FEATURE [Part::Part2DObjectPython] Rectangle068  # Draft 2D object (typed FeaturePython)
  Area = 0
  ChamferSize = 0
  Columns = 1
  FilletRadius = 0
  Height = 6
  Length = 6
  MakeFace = false
  Placement = pos=(34.7128,-276.025,0) rot=(0,0,1;1.92981rad)
  Rows = 1
FEATURE [Part::Part2DObjectPython] Circle068  # Draft 2D object (typed FeaturePython)
  Area = 1.13097
  FirstAngle = 0
  LastAngle = 0
  MakeFace = true
  Placement = pos=(29.5851,-270.9,0) rot=(0,0,1;1.92981rad)
  Radius = 0.6
FEATURE [Part::Part2DObjectPython] Rectangle069  # Draft 2D object (typed FeaturePython)
  Area = 0
  ChamferSize = 0
  Columns = 1
  FilletRadius = 0
  Height = 6
  Length = 6
  MakeFace = false
  Placement = pos=(50.2362,-273.252,0) rot=(0,0,1;2.08375rad)
  Rows = 1
FEATURE [Part::Part2DObjectPython] Circle069  # Draft 2D object (typed FeaturePython)
  Area = 1.13097
  FirstAngle = 0
  LastAngle = 0
  MakeFace = true
  Placement = pos=(44.3833,-268.973,0) rot=(0,0,1;2.08375rad)
  Radius = 0.6
FEATURE [Part::Part2DObjectPython] Rectangle070  # Draft 2D object (typed FeaturePython)
  Area = 0
  ChamferSize = 0
  Columns = 1
  FilletRadius = 0
  Height = 6
  Length = 6
  MakeFace = false
  Placement = pos=(100.186,-257.625,0) rot=(0,0,1;2.61957rad)
  Rows = 1
FEATURE [App::FeaturePython] Text020  # WARN: FeaturePython — macro-defined, semantics opaque (R4)
  Placement = pos=(89.1931,-261.188,0) rot=(0,0,-1;5.78612rad)
  Text = 0
FEATURE [App::FeaturePython] Text021  # WARN: FeaturePython — macro-defined, semantics opaque (R4)
  Placement = pos=(176.926,-207.363,0) rot=(0,0,1;1.57691rad)
  Text = 4
FEATURE [Part::Part2DObjectPython] Circle070  # Draft 2D object (typed FeaturePython)
  Area = 1.13097
  FirstAngle = 0
  LastAngle = 0
  MakeFace = true
  Placement = pos=(92.9695,-256.935,0) rot=(0,0,1;2.61957rad)
  Radius = 0.6
FEATURE [Part::Part2DObjectPython] Rectangle071  # Draft 2D object (typed FeaturePython)
  Area = 0
  ChamferSize = 0
  Columns = 1
  FilletRadius = 0
  Height = 6
  Length = 6
  MakeFace = false
  Placement = pos=(114.274,-251.175,0) rot=(0,0,1;2.78781rad)
  Rows = 1
FEATURE [Part::Part2DObjectPython] Circle071  # Draft 2D object (typed FeaturePython)
  Area = 1.13097
  FirstAngle = 0
  LastAngle = 0
  MakeFace = true
  Placement = pos=(107.043,-251.703,0) rot=(0,0,1;2.78781rad)
  Radius = 0.6
FEATURE [Part::Part2DObjectPython] Rectangle072  # Draft 2D object (typed FeaturePython)
  Area = 0
  ChamferSize = 0
  Columns = 1
  FilletRadius = 0
  Height = 6
  Length = 6
  MakeFace = false
  Placement = pos=(127.902,-243.961,0) rot=(0,0,1;2.96008rad)
  Rows = 1
FEATURE [Part::Part2DObjectPython] Circle072  # Draft 2D object (typed FeaturePython)
  Area = 1.13097
  FirstAngle = 0
  LastAngle = 0
  MakeFace = true
  Placement = pos=(120.869,-245.72,0) rot=(0,0,1;2.96008rad)
  Radius = 0.6
FEATURE [Part::Part2DObjectPython] Rectangle073  # Draft 2D object (typed FeaturePython)
  Area = 0
  ChamferSize = 0
  Columns = 1
  FilletRadius = 0
  Height = 6
  Length = 6
  MakeFace = false
  Placement = pos=(141.016,-236.036,0) rot=(0,0,1;3.13636rad)
  Rows = 1
FEATURE [Part::Part2DObjectPython] Circle073  # Draft 2D object (typed FeaturePython)
  Area = 1.13097
  FirstAngle = 0
  LastAngle = 0
  MakeFace = true
  Placement = pos=(134.4,-239.001,0) rot=(0,0,1;3.13636rad)
  Radius = 0.6
FEATURE [Part::Part2DObjectPython] Rectangle074  # Draft 2D object (typed FeaturePython)
  Area = 0
  ChamferSize = 0
  Columns = 1
  FilletRadius = 0
  Height = 6
  Length = 6
  MakeFace = false
  Placement = pos=(153.592,-227.443,0) rot=(0,0,1;3.31665rad)
  Rows = 1
FEATURE [Part::Part2DObjectPython] Circle074  # Draft 2D object (typed FeaturePython)
  Area = 1.13097
  FirstAngle = 0
  LastAngle = 0
  MakeFace = true
  Placement = pos=(147.615,-231.547,0) rot=(0,0,1;3.31665rad)
  Radius = 0.6
FEATURE [Part::Part2DObjectPython] Rectangle075  # Draft 2D object (typed FeaturePython)
  Area = 0
  ChamferSize = 0
  Columns = 1
  FilletRadius = 0
  Height = 6
  Length = 6
  MakeFace = false
  Placement = pos=(165.62,-218.244,0) rot=(0,0,1;3.49659rad)
  Rows = 1
FEATURE [Part::Part2DObjectPython] Circle075  # Draft 2D object (typed FeaturePython)
  Area = 1.13097
  FirstAngle = 0
  LastAngle = 0
  MakeFace = true
  Placement = pos=(160.474,-223.351,0) rot=(0,0,1;3.49659rad)
  Radius = 0.6
FEATURE [Part::Part2DObjectPython] Rectangle076  # Draft 2D object (typed FeaturePython)
  Area = 0
  ChamferSize = 0
  Columns = 1
  FilletRadius = 0
  Height = 6
  Length = 6
  MakeFace = false
  Placement = pos=(177.079,-208.472,0) rot=(0,0,1;3.67479rad)
  Rows = 1
FEATURE [Part::Part2DObjectPython] Circle076  # Draft 2D object (typed FeaturePython)
  Area = 1.13097
  FirstAngle = 0
  LastAngle = 0
  MakeFace = true
  Placement = pos=(172.92,-214.41,0) rot=(0,0,1;3.67479rad)
  Radius = 0.6
FEATURE [Part::Part2DObjectPython] Rectangle077  # Draft 2D object (typed FeaturePython)
  Area = 0
  ChamferSize = 0
  Columns = 1
  FilletRadius = 0
  Height = 6
  Length = 6
  MakeFace = false
  Placement = pos=(211.679,-171.874,0) rot=(0,0,1;4.14097rad)
  Rows = 1
FEATURE [App::FeaturePython] Text022  # WARN: FeaturePython — macro-defined, semantics opaque (R4)
  Placement = pos=(207.836,-181.597,0) rot=(0,0,-1;5.26252rad)
  Text = 0
FEATURE [App::FeaturePython] Text023  # WARN: FeaturePython — macro-defined, semantics opaque (R4)
  Placement = pos=(256.902,-91.1209,0) rot=(0,0,1;2.1005rad)
  Text = 5
FEATURE [Part::Part2DObjectPython] Circle077  # Draft 2D object (typed FeaturePython)
  Area = 1.13097
  FirstAngle = 0
  LastAngle = 0
  MakeFace = true
  Placement = pos=(210.633,-179.048,0) rot=(0,0,1;4.14097rad)
  Radius = 0.6
FEATURE [Part::Part2DObjectPython] Rectangle078  # Draft 2D object (typed FeaturePython)
  Area = 0
  ChamferSize = 0
  Columns = 1
  FilletRadius = 0
  Height = 6
  Length = 6
  MakeFace = false
  Placement = pos=(224.524,-160.368,0) rot=(0,0,1;3.31874rad)
  Rows = 1
FEATURE [Part::Part2DObjectPython] Circle078  # Draft 2D object (typed FeaturePython)
  Area = 1.13097
  FirstAngle = 0
  LastAngle = 0
  MakeFace = true
  Placement = pos=(218.556,-164.484,0) rot=(0,0,1;3.31874rad)
  Radius = 0.6
FEATURE [Part::Part2DObjectPython] Rectangle079  # Draft 2D object (typed FeaturePython)
  Area = 0
  ChamferSize = 0
  Columns = 1
  FilletRadius = 0
  Height = 6
  Length = 6
  MakeFace = false
  Placement = pos=(233.417,-154.59,0) rot=(0,0,1;1.41476rad)
  Rows = 1
FEATURE [Part::Part2DObjectPython] Circle079  # Draft 2D object (typed FeaturePython)
  Area = 1.13097
  FirstAngle = 0
  LastAngle = 0
  MakeFace = true
  Placement = pos=(231.479,-147.604,0) rot=(0,0,1;1.41476rad)
  Radius = 0.6
FEATURE [Part::Part2DObjectPython] Rectangle080  # Draft 2D object (typed FeaturePython)
  Area = 0
  ChamferSize = 0
  Columns = 1
  FilletRadius = 0
  Height = 6
  Length = 6
  MakeFace = false
  Placement = pos=(241.673,-141.311,0) rot=(0,0,1;1.46084rad)
  Rows = 1
FEATURE [Part::Part2DObjectPython] Circle080  # Draft 2D object (typed FeaturePython)
  Area = 1.13097
  FirstAngle = 0
  LastAngle = 0
  MakeFace = true
  Placement = pos=(239.415,-134.422,0) rot=(0,0,1;1.46084rad)
  Radius = 0.6
FEATURE [Part::Part2DObjectPython] Rectangle081  # Draft 2D object (typed FeaturePython)
  Area = 0
  ChamferSize = 0
  Columns = 1
  FilletRadius = 0
  Height = 6
  Length = 6
  MakeFace = false
  Placement = pos=(249.26,-127.516,0) rot=(0,0,1;1.53484rad)
  Rows = 1
FEATURE [Part::Part2DObjectPython] Circle081  # Draft 2D object (typed FeaturePython)
  Area = 1.13097
  FirstAngle = 0
  LastAngle = 0
  MakeFace = true
  Placement = pos=(246.499,-120.812,0) rot=(0,0,1;1.53484rad)
  Radius = 0.6
FEATURE [Part::Part2DObjectPython] Rectangle082  # Draft 2D object (typed FeaturePython)
  Area = 0
  ChamferSize = 0
  Columns = 1
  FilletRadius = 0
  Height = 6
  Length = 6
  MakeFace = false
  Placement = pos=(256.074,-113.29,0) rot=(0,0,1;1.61321rad)
  Rows = 1
FEATURE [Part::Part2DObjectPython] Circle082  # Draft 2D object (typed FeaturePython)
  Area = 1.13097
  FirstAngle = 0
  LastAngle = 0
  MakeFace = true
  Placement = pos=(252.797,-106.823,0) rot=(0,0,1;1.61321rad)
  Radius = 0.6
FEATURE [Part::Part2DObjectPython] Rectangle083  # Draft 2D object (typed FeaturePython)
  Area = 0
  ChamferSize = 0
  Columns = 1
  FilletRadius = 0
  Height = 6
  Length = 6
  MakeFace = false
  Placement = pos=(262.079,-98.695,0) rot=(0,0,1;1.69506rad)
  Rows = 1
FEATURE [Part::Part2DObjectPython] Circle083  # Draft 2D object (typed FeaturePython)
  Area = 1.13097
  FirstAngle = 0
  LastAngle = 0
  MakeFace = true
  Placement = pos=(258.284,-92.5178,0) rot=(0,0,1;1.69506rad)
  Radius = 0.6
FEATURE [App::DocumentObjectGroup] Everything
  Group = -> [Rectangle,Circle,Rectangle001,Circle001,Rectangle002,Circle002,Rectangle003,Circle003,Rectangle004,Circle004,Rectangle005,Circle005,Rectangle006,Circle006,Rectangle007,Circle007,Rectangle008,Circle008,Rectangle009,Circle009,Rectangle010,Circle010,Rectangle011,Circle011,Rectangle012,Circle012,Rectangle013,Circle013,Rectangle014,Circle014,Rectangle015,Circle015,Rectangle016,Circle016,Rectangle017,+133 more]
FEATURE [Part::Part2DObjectPython] Rectangle084  # Draft 2D object (typed FeaturePython)
  Area = 0
  ChamferSize = 0
  Columns = 1
  FilletRadius = 0
  Height = 6
  Length = 6
  MakeFace = false
  Placement = pos=(275.479,-48.7292,0) rot=(0,0,1;1.70274rad)
  Rows = 1
FEATURE [App::FeaturePython] Text024  # WARN: FeaturePython — macro-defined, semantics opaque (R4)
  Placement = pos=(270.79,-53.3517,0) rot=(0,0,-1;4.73892rad)
  Text = 0
FEATURE [App::FeaturePython] Text025  # WARN: FeaturePython — macro-defined, semantics opaque (R4)
  Placement = pos=(268.047,49.5386,0) rot=(0,0,1;2.6241rad)
  Text = 6.
FEATURE [Part::Part2DObjectPython] Circle084  # Draft 2D object (typed FeaturePython)
  Area = 1.13097
  FirstAngle = 0
  LastAngle = 0
  MakeFace = true
  Placement = pos=(271.636,-42.5813,0) rot=(0,0,1;1.70274rad)
  Radius = 0.6
FEATURE [Part::Part2DObjectPython] Rectangle085  # Draft 2D object (typed FeaturePython)
  Area = 0
  ChamferSize = 0
  Columns = 1
  FilletRadius = 0
  Height = 6
  Length = 6
  MakeFace = false
  Placement = pos=(277.675,-33.3808,0) rot=(0,0,1;1.71705rad)
  Rows = 1
FEATURE [Part::Part2DObjectPython] Circle085  # Draft 2D object (typed FeaturePython)
  Area = 1.13097
  FirstAngle = 0
  LastAngle = 0
  MakeFace = true
  Placement = pos=(273.745,-27.2884,0) rot=(0,0,1;1.71705rad)
  Radius = 0.6
FEATURE [Part::Part2DObjectPython] Rectangle086  # Draft 2D object (typed FeaturePython)
  Area = 0
  ChamferSize = 0
  Columns = 1
  FilletRadius = 0
  Height = 6
  Length = 6
  MakeFace = false
  Placement = pos=(278.941,-18.0257,0) rot=(0,0,1;1.70379rad)
  Rows = 1
FEATURE [Part::Part2DObjectPython] Circle086  # Draft 2D object (typed FeaturePython)
  Area = 1.13097
  FirstAngle = 0
  LastAngle = 0
  MakeFace = true
  Placement = pos=(275.093,-11.8818,0) rot=(0,0,1;1.70379rad)
  Radius = 0.6
FEATURE [Part::Part2DObjectPython] Rectangle087  # Draft 2D object (typed FeaturePython)
  Area = 0
  ChamferSize = 0
  Columns = 1
  FilletRadius = 0
  Height = 6
  Length = 6
  MakeFace = false
  Placement = pos=(279.274,-2.69808,0) rot=(0,0,1;1.66696rad)
  Rows = 1
FEATURE [Part::Part2DObjectPython] Circle087  # Draft 2D object (typed FeaturePython)
  Area = 1.13097
  FirstAngle = 0
  LastAngle = 0
  MakeFace = true
  Placement = pos=(275.654,3.58337,0) rot=(0,0,1;1.66696rad)
  Radius = 0.6
FEATURE [Part::Part2DObjectPython] Rectangle088  # Draft 2D object (typed FeaturePython)
  Area = 0
  ChamferSize = 0
  Columns = 1
  FilletRadius = 0
  Height = 6
  Length = 6
  MakeFace = false
  Placement = pos=(278.705,12.5914,0) rot=(0,0,1;1.61687rad)
  Rows = 1
FEATURE [Part::Part2DObjectPython] Circle088  # Draft 2D object (typed FeaturePython)
  Area = 1.13097
  FirstAngle = 0
  LastAngle = 0
  MakeFace = true
  Placement = pos=(275.404,19.0462,0) rot=(0,0,1;1.61687rad)
  Radius = 0.6
FEATURE [Part::Part2DObjectPython] Rectangle089  # Draft 2D object (typed FeaturePython)
  Area = 0
  ChamferSize = 0
  Columns = 1
  FilletRadius = 0
  Height = 6
  Length = 6
  MakeFace = false
  Placement = pos=(277.289,27.8694,0) rot=(0,0,1;1.57725rad)
  Rows = 1
FEATURE [Part::Part2DObjectPython] Circle089  # Draft 2D object (typed FeaturePython)
  Area = 1.13097
  FirstAngle = 0
  LastAngle = 0
  MakeFace = true
  Placement = pos=(274.247,34.4499,0) rot=(0,0,1;1.57725rad)
  Radius = 0.6
FEATURE [Part::Part2DObjectPython] Rectangle090  # Draft 2D object (typed FeaturePython)
  Area = 0
  ChamferSize = 0
  Columns = 1
  FilletRadius = 0
  Height = 6
  Length = 6
  MakeFace = false
  Placement = pos=(275.114,43.1542,0) rot=(0,0,1;1.57219rad)
  Rows = 1
FEATURE [Part::Part2DObjectPython] Circle090  # Draft 2D object (typed FeaturePython)
  Area = 1.13097
  FirstAngle = 0
  LastAngle = 0
  MakeFace = true
  Placement = pos=(272.105,49.75,0) rot=(0,0,1;1.57219rad)
  Radius = 0.6
FEATURE [Part::Part2DObjectPython] Rectangle091  # Draft 2D object (typed FeaturePython)
  Area = 0
  ChamferSize = 0
  Columns = 1
  FilletRadius = 0
  Height = 6
  Length = 6
  MakeFace = false
  Placement = pos=(262.623,94.4037,0) rot=(0,0,1;1.94744rad)
  Rows = 1
FEATURE [App::FeaturePython] Text026  # WARN: FeaturePython — macro-defined, semantics opaque (R4)
  Placement = pos=(261.188,89.1931,0) rot=(0,0,-1;4.21532rad)
  Text = 0
FEATURE [App::FeaturePython] Text027  # WARN: FeaturePython — macro-defined, semantics opaque (R4)
  Placement = pos=(207.363,176.926,0) rot=(0,0,1;3.1477rad)
  Text = 7
FEATURE [Part::Part2DObjectPython] Circle091  # Draft 2D object (typed FeaturePython)
  Area = 1.13097
  FirstAngle = 0
  LastAngle = 0
  MakeFace = true
  Placement = pos=(257.406,99.4377,0) rot=(0,0,1;1.94744rad)
  Radius = 0.6
FEATURE [Part::Part2DObjectPython] Rectangle092  # Draft 2D object (typed FeaturePython)
  Area = 0
  ChamferSize = 0
  Columns = 1
  FilletRadius = 0
  Height = 6
  Length = 6
  MakeFace = false
  Placement = pos=(257.177,110.055,0) rot=(0,0,1;2.26998rad)
  Rows = 1
FEATURE [Part::Part2DObjectPython] Circle092  # Draft 2D object (typed FeaturePython)
  Area = 1.13097
  FirstAngle = 0
  LastAngle = 0
  MakeFace = true
  Placement = pos=(250.633,113.175,0) rot=(0,0,1;2.26998rad)
  Radius = 0.6
FEATURE [Part::Part2DObjectPython] Rectangle093  # Draft 2D object (typed FeaturePython)
  Area = 0
  ChamferSize = 0
  Columns = 1
  FilletRadius = 0
  Height = 6
  Length = 6
  MakeFace = false
  Placement = pos=(249.941,126.701,0) rot=(0,0,1;2.92657rad)
  Rows = 1
FEATURE [Part::Part2DObjectPython] Circle093  # Draft 2D object (typed FeaturePython)
  Area = 1.13097
  FirstAngle = 0
  LastAngle = 0
  MakeFace = true
  Placement = pos=(242.853,125.178,0) rot=(0,0,1;2.92657rad)
  Radius = 0.6
FEATURE [Part::Part2DObjectPython] Rectangle094  # Draft 2D object (typed FeaturePython)
  Area = 0
  ChamferSize = 0
  Columns = 1
  FilletRadius = 0
  Height = 6
  Length = 6
  MakeFace = false
  Placement = pos=(238.878,142.24,0) rot=(0,0,1;3.9605rad)
  Rows = 1
FEATURE [Part::Part2DObjectPython] Circle094  # Draft 2D object (typed FeaturePython)
  Area = 1.13097
  FirstAngle = 0
  LastAngle = 0
  MakeFace = true
  Placement = pos=(236.561,135.371,0) rot=(0,0,1;3.9605rad)
  Radius = 0.6
FEATURE [Part::Part2DObjectPython] Rectangle095  # Draft 2D object (typed FeaturePython)
  Area = 0
  ChamferSize = 0
  Columns = 1
  FilletRadius = 0
  Height = 6
  Length = 6
  MakeFace = false
  Placement = pos=(228.266,154.47,0) rot=(0,0,1;4.60278rad)
  Rows = 1
FEATURE [Part::Part2DObjectPython] Circle095  # Draft 2D object (typed FeaturePython)
  Area = 1.13097
  FirstAngle = 0
  LastAngle = 0
  MakeFace = true
  Placement = pos=(230.526,147.582,0) rot=(0,0,1;4.60278rad)
  Radius = 0.6
FEATURE [Part::Part2DObjectPython] Rectangle096  # Draft 2D object (typed FeaturePython)
  Area = 0
  ChamferSize = 0
  Columns = 1
  FilletRadius = 0
  Height = 6
  Length = 6
  MakeFace = false
  Placement = pos=(219.1,160.85,0) rot=(0,0,1;0rad)
  Rows = 1
FEATURE [Part::Part2DObjectPython] Circle096  # Draft 2D object (typed FeaturePython)
  Area = 1.13097
  FirstAngle = 0
  LastAngle = 0
  MakeFace = true
  Placement = pos=(225.7,163.85,0) rot=(0,0,1;0rad)
  Radius = 0.6
FEATURE [Part::Part2DObjectPython] Rectangle097  # Draft 2D object (typed FeaturePython)
  Area = 0
  ChamferSize = 0
  Columns = 1
  FilletRadius = 0
  Height = 6
  Length = 6
  MakeFace = false
  Placement = pos=(209.58,173.02,0) rot=(0,0,1;0rad)
  Rows = 1
FEATURE [Part::Part2DObjectPython] Circle097  # Draft 2D object (typed FeaturePython)
  Area = 1.13097
  FirstAngle = 0
  LastAngle = 0
  MakeFace = true
  Placement = pos=(216.18,176.02,0) rot=(0,0,1;0rad)
  Radius = 0.6
FEATURE [Part::Part2DObjectPython] Rectangle098  # Draft 2D object (typed FeaturePython)
  Area = 0
  ChamferSize = 0
  Columns = 1
  FilletRadius = 0
  Height = 6
  Length = 6
  MakeFace = false
  Placement = pos=(173.02,209.58,0) rot=(0,0,1;0rad)
  Rows = 1
FEATURE [App::FeaturePython] Text028  # WARN: FeaturePython — macro-defined, semantics opaque (R4)
  Placement = pos=(181.597,207.836,0) rot=(0,0,-1;3.69172rad)
  Text = 0
FEATURE [App::FeaturePython] Text029  # WARN: FeaturePython — macro-defined, semantics opaque (R4)
  Placement = pos=(91.1209,256.902,0) rot=(0,0,1;3.6713rad)
  Text = 8
FEATURE [Part::Part2DObjectPython] Circle098  # Draft 2D object (typed FeaturePython)
  Area = 1.13097
  FirstAngle = 0
  LastAngle = 0
  MakeFace = true
  Placement = pos=(179.62,212.58,0) rot=(0,0,1;0rad)
  Radius = 0.6
FEATURE [Part::Part2DObjectPython] Rectangle099  # Draft 2D object (typed FeaturePython)
  Area = 0
  ChamferSize = 0
  Columns = 1
  FilletRadius = 0
  Height = 6
  Length = 6
  MakeFace = false
  Placement = pos=(160.204,219.93,0) rot=(0,0,1;6.03465rad)
  Rows = 1
FEATURE [Part::Part2DObjectPython] Circle099  # Draft 2D object (typed FeaturePython)
  Area = 1.13097
  FirstAngle = 0
  LastAngle = 0
  MakeFace = true
  Placement = pos=(167.339,221.214,0) rot=(0,0,1;6.03465rad)
  Radius = 0.6
FEATURE [Part::Part2DObjectPython] Rectangle100  # Draft 2D object (typed FeaturePython)
  Area = 0
  ChamferSize = 0
  Columns = 1
  FilletRadius = 0
  Height = 6
  Length = 6
  MakeFace = false
  Placement = pos=(147.893,228.213,0) rot=(0,0,1;6.18981rad)
  Rows = 1
FEATURE [Part::Part2DObjectPython] Circle100  # Draft 2D object (typed FeaturePython)
  Area = 1.13097
  FirstAngle = 0
  LastAngle = 0
  MakeFace = true
  Placement = pos=(154.744,230.584,0) rot=(0,0,1;6.18981rad)
  Radius = 0.6
FEATURE [Part::Part2DObjectPython] Rectangle101  # Draft 2D object (typed FeaturePython)
  Area = 0
  ChamferSize = 0
  Columns = 1
  FilletRadius = 0
  Height = 6
  Length = 6
  MakeFace = false
  Placement = pos=(135,236.02,0) rot=(0,0,1;0rad)
  Rows = 1
FEATURE [Part::Part2DObjectPython] Circle101  # Draft 2D object (typed FeaturePython)
  Area = 1.13097
  FirstAngle = 0
  LastAngle = 0
  MakeFace = true
  Placement = pos=(141.6,239.02,0) rot=(0,0,1;0rad)
  Radius = 0.6
FEATURE [Part::Part2DObjectPython] Rectangle102  # Draft 2D object (typed FeaturePython)
  Area = 0
  ChamferSize = 0
  Columns = 1
  FilletRadius = 0
  Height = 6
  Length = 6
  MakeFace = false
  Placement = pos=(121.973,242.897,0) rot=(0,0,1;0.173486rad)
  Rows = 1
FEATURE [Part::Part2DObjectPython] Circle102  # Draft 2D object (typed FeaturePython)
  Area = 1.13097
  FirstAngle = 0
  LastAngle = 0
  MakeFace = true
  Placement = pos=(127.956,246.991,0) rot=(0,0,1;0.173486rad)
  Radius = 0.6
FEATURE [Part::Part2DObjectPython] Rectangle103  # Draft 2D object (typed FeaturePython)
  Area = 0
  ChamferSize = 0
  Columns = 1
  FilletRadius = 0
  Height = 6
  Length = 6
  MakeFace = false
  Placement = pos=(107.418,249.952,0) rot=(0,0,1;6.28266rad)
  Rows = 1
FEATURE [Part::Part2DObjectPython] Circle103  # Draft 2D object (typed FeaturePython)
  Area = 1.13097
  FirstAngle = 0
  LastAngle = 0
  MakeFace = true
  Placement = pos=(114.02,252.948,0) rot=(0,0,1;6.28266rad)
  Radius = 0.6
FEATURE [Part::Part2DObjectPython] Rectangle104  # Draft 2D object (typed FeaturePython)
  Area = 0
  ChamferSize = 0
  Columns = 1
  FilletRadius = 0
  Height = 6
  Length = 6
  MakeFace = false
  Placement = pos=(93.09,255.73,0) rot=(0,0,1;0rad)
  Rows = 1
FEATURE [Part::Part2DObjectPython] Circle104  # Draft 2D object (typed FeaturePython)
  Area = 1.13097
  FirstAngle = 0
  LastAngle = 0
  MakeFace = true
  Placement = pos=(99.69,258.73,0) rot=(0,0,1;0rad)
  Radius = 0.6
FEATURE [Part::Part2DObjectPython] Rectangle105  # Draft 2D object (typed FeaturePython)
  Area = 0
  ChamferSize = 0
  Columns = 1
  FilletRadius = 0
  Height = 6
  Length = 6
  MakeFace = false
  Placement = pos=(50.2152,273.324,0) rot=(0,0,1;2.64644rad)
  Rows = 1
FEATURE [App::FeaturePython] Text030  # WARN: FeaturePython — macro-defined, semantics opaque (R4)
  Placement = pos=(53.3517,270.79,0) rot=(0,0,-1;3.16812rad)
  Text = 0
FEATURE [App::FeaturePython] Text031  # WARN: FeaturePython — macro-defined, semantics opaque (R4)
  Placement = pos=(-49.5386,268.047,0) rot=(0,0,1;4.1949rad)
  Text = 9
FEATURE [Part::Part2DObjectPython] Circle105  # Draft 2D object (typed FeaturePython)
  Area = 1.13097
  FirstAngle = 0
  LastAngle = 0
  MakeFace = true
  Placement = pos=(42.9824,273.821,0) rot=(0,0,1;2.64644rad)
  Radius = 0.6
FEATURE [Part::Part2DObjectPython] Rectangle106  # Draft 2D object (typed FeaturePython)
  Area = 0
  ChamferSize = 0
  Columns = 1
  FilletRadius = 0
  Height = 6
  Length = 6
  MakeFace = false
  Placement = pos=(31.0661,270.033,0) rot=(0,0,1;0.836362rad)
  Rows = 1
FEATURE [Part::Part2DObjectPython] Circle106  # Draft 2D object (typed FeaturePython)
  Area = 1.13097
  FirstAngle = 0
  LastAngle = 0
  MakeFace = true
  Placement = pos=(33.2626,276.942,0) rot=(0,0,1;0.836362rad)
  Radius = 0.6
FEATURE [Part::Part2DObjectPython] Rectangle107  # Draft 2D object (typed FeaturePython)
  Area = 0
  ChamferSize = 0
  Columns = 1
  FilletRadius = 0
  Height = 6
  Length = 6
  MakeFace = false
  Placement = pos=(18.774,272.934,0) rot=(0,0,1;1.68564rad)
  Rows = 1
FEATURE [Part::Part2DObjectPython] Circle107  # Draft 2D object (typed FeaturePython)
  Area = 1.13097
  FirstAngle = 0
  LastAngle = 0
  MakeFace = true
  Placement = pos=(15.0375,279.146,0) rot=(0,0,1;1.68564rad)
  Radius = 0.6
FEATURE [Part::Part2DObjectPython] Rectangle108  # Draft 2D object (typed FeaturePython)
  Area = 0
  ChamferSize = 0
  Columns = 1
  FilletRadius = 0
  Height = 6
  Length = 6
  MakeFace = false
  Placement = pos=(3.92786,274.396,0) rot=(0,0,1;1.96856rad)
  Rows = 1
FEATURE [Part::Part2DObjectPython] Circle108  # Draft 2D object (typed FeaturePython)
  Area = 1.13097
  FirstAngle = 0
  LastAngle = 0
  MakeFace = true
  Placement = pos=(-1.39448,279.319,0) rot=(0,0,1;1.96856rad)
  Radius = 0.6
FEATURE [Part::Part2DObjectPython] Rectangle109  # Draft 2D object (typed FeaturePython)
  Area = 0
  ChamferSize = 0
  Columns = 1
  FilletRadius = 0
  Height = 6
  Length = 6
  MakeFace = false
  Placement = pos=(-11.3587,274.447,0) rot=(0,0,1;2.08829rad)
  Rows = 1
FEATURE [Part::Part2DObjectPython] Circle109  # Draft 2D object (typed FeaturePython)
  Area = 1.13097
  FirstAngle = 0
  LastAngle = 0
  MakeFace = true
  Placement = pos=(-17.2309,278.699,0) rot=(0,0,1;2.08829rad)
  Radius = 0.6
FEATURE [Part::Part2DObjectPython] Rectangle110  # Draft 2D object (typed FeaturePython)
  Area = 0
  ChamferSize = 0
  Columns = 1
  FilletRadius = 0
  Height = 6
  Length = 6
  MakeFace = false
  Placement = pos=(-26.6676,273.557,0) rot=(0,0,1;2.18742rad)
  Rows = 1
FEATURE [Part::Part2DObjectPython] Circle110  # Draft 2D object (typed FeaturePython)
  Area = 1.13097
  FirstAngle = 0
  LastAngle = 0
  MakeFace = true
  Placement = pos=(-32.9318,277.207,0) rot=(0,0,1;2.18742rad)
  Radius = 0.6
FEATURE [Part::Part2DObjectPython] Rectangle111  # Draft 2D object (typed FeaturePython)
  Area = 0
  ChamferSize = 0
  Columns = 1
  FilletRadius = 0
  Height = 6
  Length = 6
  MakeFace = false
  Placement = pos=(-41.9186,271.801,0) rot=(0,0,1;2.28324rad)
  Rows = 1
FEATURE [Part::Part2DObjectPython] Circle111  # Draft 2D object (typed FeaturePython)
  Area = 1.13097
  FirstAngle = 0
  LastAngle = 0
  MakeFace = true
  Placement = pos=(-48.5033,274.834,0) rot=(0,0,1;2.28324rad)
  Radius = 0.6
FEATURE [Part::Part2DObjectPython] Rectangle112  # Draft 2D object (typed FeaturePython)
  Area = 0
  ChamferSize = 0
  Columns = 1
  FilletRadius = 0
  Height = 6
  Length = 6
  MakeFace = false
  Placement = pos=(-92.0023,259.866,0) rot=(0,0,1;2.62724rad)
  Rows = 1
FEATURE [App::FeaturePython] Text032  # WARN: FeaturePython — macro-defined, semantics opaque (R4)
  Placement = pos=(-89.1931,261.188,0) rot=(0,0,-1;2.64452rad)
  Text = 0
FEATURE [App::FeaturePython] Text033  # WARN: FeaturePython — macro-defined, semantics opaque (R4)
  Placement = pos=(-176.926,207.363,0) rot=(0,0,1;4.7185rad)
  Text = 10
FEATURE [Part::Part2DObjectPython] Circle112  # Draft 2D object (typed FeaturePython)
  Area = 1.13097
  FirstAngle = 0
  LastAngle = 0
  MakeFace = true
  Placement = pos=(-99.2242,260.501,0) rot=(0,0,1;2.62724rad)
  Radius = 0.6
FEATURE [Part::Part2DObjectPython] Rectangle113  # Draft 2D object (typed FeaturePython)
  Area = 0
  ChamferSize = 0
  Columns = 1
  FilletRadius = 0
  Height = 6
  Length = 6
  MakeFace = false
  Placement = pos=(-106.492,254.554,0) rot=(0,0,1;2.74383rad)
  Rows = 1
FEATURE [Part::Part2DObjectPython] Circle113  # Draft 2D object (typed FeaturePython)
  Area = 1.13097
  FirstAngle = 0
  LastAngle = 0
  MakeFace = true
  Placement = pos=(-113.739,254.344,0) rot=(0,0,1;2.74383rad)
  Radius = 0.6
FEATURE [Part::Part2DObjectPython] Rectangle114  # Draft 2D object (typed FeaturePython)
  Area = 0
  ChamferSize = 0
  Columns = 1
  FilletRadius = 0
  Height = 6
  Length = 6
  MakeFace = false
  Placement = pos=(-120.717,248.458,0) rot=(0,0,1;2.87072rad)
  Rows = 1
FEATURE [Part::Part2DObjectPython] Circle114  # Draft 2D object (typed FeaturePython)
  Area = 1.13097
  FirstAngle = 0
  LastAngle = 0
  MakeFace = true
  Placement = pos=(-127.879,247.333,0) rot=(0,0,1;2.87072rad)
  Radius = 0.6
FEATURE [Part::Part2DObjectPython] Rectangle115  # Draft 2D object (typed FeaturePython)
  Area = 0
  ChamferSize = 0
  Columns = 1
  FilletRadius = 0
  Height = 6
  Length = 6
  MakeFace = false
  Placement = pos=(-134.632,241.6,0) rot=(0,0,1;3.00982rad)
  Rows = 1
FEATURE [Part::Part2DObjectPython] Circle115  # Draft 2D object (typed FeaturePython)
  Area = 1.13097
  FirstAngle = 0
  LastAngle = 0
  MakeFace = true
  Placement = pos=(-141.569,239.493,0) rot=(0,0,1;3.00982rad)
  Radius = 0.6
FEATURE [Part::Part2DObjectPython] Rectangle116  # Draft 2D object (typed FeaturePython)
  Area = 0
  ChamferSize = 0
  Columns = 1
  FilletRadius = 0
  Height = 6
  Length = 6
  MakeFace = false
  Placement = pos=(-148.226,233.984,0) rot=(0,0,1;3.16323rad)
  Rows = 1
FEATURE [Part::Part2DObjectPython] Circle116  # Draft 2D object (typed FeaturePython)
  Area = 1.13097
  FirstAngle = 0
  LastAngle = 0
  MakeFace = true
  Placement = pos=(-154.759,230.842,0) rot=(0,0,1;3.16323rad)
  Radius = 0.6
FEATURE [Part::Part2DObjectPython] Rectangle117  # Draft 2D object (typed FeaturePython)
  Area = 0
  ChamferSize = 0
  Columns = 1
  FilletRadius = 0
  Height = 6
  Length = 6
  MakeFace = false
  Placement = pos=(-161.479,225.619,0) rot=(0,0,1;3.3341rad)
  Rows = 1
FEATURE [Part::Part2DObjectPython] Circle117  # Draft 2D object (typed FeaturePython)
  Area = 1.13097
  FirstAngle = 0
  LastAngle = 0
  MakeFace = true
  Placement = pos=(-167.383,221.411,0) rot=(0,0,1;3.3341rad)
  Radius = 0.6
FEATURE [Part::Part2DObjectPython] Rectangle118  # Draft 2D object (typed FeaturePython)
  Area = 0
  ChamferSize = 0
  Columns = 1
  FilletRadius = 0
  Height = 6
  Length = 6
  MakeFace = false
  Placement = pos=(-174.366,216.487,0) rot=(0,0,1;3.52644rad)
  Rows = 1
FEATURE [Part::Part2DObjectPython] Circle118  # Draft 2D object (typed FeaturePython)
  Area = 1.13097
  FirstAngle = 0
  LastAngle = 0
  MakeFace = true
  Placement = pos=(-179.357,211.229,0) rot=(0,0,1;3.52644rad)
  Radius = 0.6
FEATURE [Part::Part2DObjectPython] Rectangle119  # Draft 2D object (typed FeaturePython)
  Area = 0
  ChamferSize = 0
  Columns = 1
  FilletRadius = 0
  Height = 6
  Length = 6
  MakeFace = false
  Placement = pos=(-214.605,179.748,0) rot=(0,0,1;4.42458rad)
  Rows = 1
FEATURE [App::FeaturePython] Text034  # WARN: FeaturePython — macro-defined, semantics opaque (R4)
  Placement = pos=(-207.836,181.597,0) rot=(0,0,-1;2.12092rad)
  Text = 0
FEATURE [App::FeaturePython] Text035  # WARN: FeaturePython — macro-defined, semantics opaque (R4)
  Placement = pos=(-256.902,91.1209,0) rot=(0,0,1;5.2421rad)
  Text = 11
FEATURE [Part::Part2DObjectPython] Circle119  # Draft 2D object (typed FeaturePython)
  Area = 1.13097
  FirstAngle = 0
  LastAngle = 0
  MakeFace = true
  Placement = pos=(-213.602,172.568,0) rot=(0,0,1;4.42458rad)
  Radius = 0.6
FEATURE [Part::Part2DObjectPython] Rectangle120  # Draft 2D object (typed FeaturePython)
  Area = 0
  ChamferSize = 0
  Columns = 1
  FilletRadius = 0
  Height = 6
  Length = 6
  MakeFace = false
  Placement = pos=(-225.1,160.85,0) rot=(0,0,1;0rad)
  Rows = 1
FEATURE [Part::Part2DObjectPython] Circle120  # Draft 2D object (typed FeaturePython)
  Area = 1.13097
  FirstAngle = 0
  LastAngle = 0
  MakeFace = true
  Placement = pos=(-218.5,163.85,0) rot=(0,0,1;0rad)
  Radius = 0.6
FEATURE [Part::Part2DObjectPython] Rectangle121  # Draft 2D object (typed FeaturePython)
  Area = 0
  ChamferSize = 0
  Columns = 1
  FilletRadius = 0
  Height = 6
  Length = 6
  MakeFace = false
  Placement = pos=(-235.048,152.14,0) rot=(0,0,1;5.26479rad)
  Rows = 1
FEATURE [Part::Part2DObjectPython] Circle121  # Draft 2D object (typed FeaturePython)
  Area = 1.13097
  FirstAngle = 0
  LastAngle = 0
  MakeFace = true
  Placement = pos=(-229.031,148.095,0) rot=(0,0,1;5.26479rad)
  Radius = 0.6
FEATURE [Part::Part2DObjectPython] Rectangle122  # Draft 2D object (typed FeaturePython)
  Area = 0
  ChamferSize = 0
  Columns = 1
  FilletRadius = 0
  Height = 6
  Length = 6
  MakeFace = false
  Placement = pos=(-243.133,136.961,0) rot=(0,0,1;5.74528rad)
  Rows = 1
FEATURE [Part::Part2DObjectPython] Circle122  # Draft 2D object (typed FeaturePython)
  Area = 1.13097
  FirstAngle = 0
  LastAngle = 0
  MakeFace = true
  Placement = pos=(-235.928,136.156,0) rot=(0,0,1;5.74528rad)
  Radius = 0.6
FEATURE [Part::Part2DObjectPython] Rectangle123  # Draft 2D object (typed FeaturePython)
  Area = 0
  ChamferSize = 0
  Columns = 1
  FilletRadius = 0
  Height = 6
  Length = 6
  MakeFace = false
  Placement = pos=(-249.61,121.67,0) rot=(0,0,1;6.19976rad)
  Rows = 1
FEATURE [Part::Part2DObjectPython] Circle123  # Draft 2D object (typed FeaturePython)
  Area = 1.13097
  FirstAngle = 0
  LastAngle = 0
  MakeFace = true
  Placement = pos=(-242.783,124.11,0) rot=(0,0,1;6.19976rad)
  Radius = 0.6
FEATURE [Part::Part2DObjectPython] Rectangle124  # Draft 2D object (typed FeaturePython)
  Area = 0
  ChamferSize = 0
  Columns = 1
  FilletRadius = 0
  Height = 6
  Length = 6
  MakeFace = false
  Placement = pos=(-255.95,107.42,0) rot=(0,0,1;0rad)
  Rows = 1
FEATURE [Part::Part2DObjectPython] Circle124  # Draft 2D object (typed FeaturePython)
  Area = 1.13097
  FirstAngle = 0
  LastAngle = 0
  MakeFace = true
  Placement = pos=(-249.35,110.42,0) rot=(0,0,1;0rad)
  Radius = 0.6
FEATURE [Part::Part2DObjectPython] Rectangle125  # Draft 2D object (typed FeaturePython)
  Area = 0
  ChamferSize = 0
  Columns = 1
  FilletRadius = 0
  Height = 6
  Length = 6
  MakeFace = false
  Placement = pos=(-261.73,93.09,0) rot=(0,0,1;0rad)
  Rows = 1
FEATURE [Part::Part2DObjectPython] Circle125  # Draft 2D object (typed FeaturePython)
  Area = 1.13097
  FirstAngle = 0
  LastAngle = 0
  MakeFace = true
  Placement = pos=(-255.13,96.09,0) rot=(0,0,1;0rad)
  Radius = 0.6
FEATURE [Part::Part2DObjectPython] Rectangle126  # Draft 2D object (typed FeaturePython)
  Area = 0
  ChamferSize = 0
  Columns = 1
  FilletRadius = 0
  Height = 6
  Length = 6
  MakeFace = false
  Placement = pos=(-275.11,43.15,0) rot=(0,0,1;0rad)
  Rows = 1
FEATURE [App::FeaturePython] Text036  # WARN: FeaturePython — macro-defined, semantics opaque (R4)
  Placement = pos=(-270.79,53.3517,0) rot=(0,0,-1;1.59733rad)
  Text = 0
FEATURE [App::FeaturePython] Text037  # WARN: FeaturePython — macro-defined, semantics opaque (R4)
  Placement = pos=(-268.047,-49.5386,0) rot=(0,0,1;5.7657rad)
  Text = 12
FEATURE [Part::Part2DObjectPython] Circle126  # Draft 2D object (typed FeaturePython)
  Area = 1.13097
  FirstAngle = 0
  LastAngle = 0
  MakeFace = true
  Placement = pos=(-268.51,46.15,0) rot=(0,0,1;0rad)
  Radius = 0.6
FEATURE [Part::Part2DObjectPython] Rectangle127  # Draft 2D object (typed FeaturePython)
  Area = 0
  ChamferSize = 0
  Columns = 1
  FilletRadius = 0
  Height = 6
  Length = 6
  MakeFace = false
  Placement = pos=(-277.27,27.85,0) rot=(0,0,1;0rad)
  Rows = 1
FEATURE [Part::Part2DObjectPython] Circle127  # Draft 2D object (typed FeaturePython)
  Area = 1.13097
  FirstAngle = 0
  LastAngle = 0
  MakeFace = true
  Placement = pos=(-270.67,30.85,0) rot=(0,0,1;0rad)
  Radius = 0.6
FEATURE [Part::Part2DObjectPython] Rectangle128  # Draft 2D object (typed FeaturePython)
  Area = 0
  ChamferSize = 0
  Columns = 1
  FilletRadius = 0
  Height = 6
  Length = 6
  MakeFace = false
  Placement = pos=(-278.57,12.45,0) rot=(0,0,1;0rad)
  Rows = 1
FEATURE [Part::Part2DObjectPython] Circle128  # Draft 2D object (typed FeaturePython)
  Area = 1.13097
  FirstAngle = 0
  LastAngle = 0
  MakeFace = true
  Placement = pos=(-271.97,15.45,0) rot=(0,0,1;0rad)
  Radius = 0.6
FEATURE [Part::Part2DObjectPython] Rectangle129  # Draft 2D object (typed FeaturePython)
  Area = 0
  ChamferSize = 0
  Columns = 1
  FilletRadius = 0
  Height = 6
  Length = 6
  MakeFace = false
  Placement = pos=(-271.98,-1.35533,0) rot=(0,0,1;2.03104rad)
  Rows = 1
FEATURE [Part::Part2DObjectPython] Circle129  # Draft 2D object (typed FeaturePython)
  Area = 1.13097
  FirstAngle = 0
  LastAngle = 0
  MakeFace = true
  Placement = pos=(-277.599,3.2254,0) rot=(0,0,1;2.03104rad)
  Radius = 0.6
FEATURE [Part::Part2DObjectPython] Rectangle130  # Draft 2D object (typed FeaturePython)
  Area = 0
  ChamferSize = 0
  Columns = 1
  FilletRadius = 0
  Height = 6
  Length = 6
  MakeFace = false
  Placement = pos=(-271.405,-16.2603,0) rot=(0,0,1;2.16403rad)
  Rows = 1
FEATURE [Part::Part2DObjectPython] Circle130  # Draft 2D object (typed FeaturePython)
  Area = 1.13097
  FirstAngle = 0
  LastAngle = 0
  MakeFace = true
  Placement = pos=(-277.583,-12.4651,0) rot=(0,0,1;2.16403rad)
  Radius = 0.6
FEATURE [Part::Part2DObjectPython] Rectangle131  # Draft 2D object (typed FeaturePython)
  Area = 0
  ChamferSize = 0
  Columns = 1
  FilletRadius = 0
  Height = 6
  Length = 6
  MakeFace = false
  Placement = pos=(-270.043,-31.2094,0) rot=(0,0,1;2.27137rad)
  Rows = 1
FEATURE [Part::Part2DObjectPython] Circle131  # Draft 2D object (typed FeaturePython)
  Area = 1.13097
  FirstAngle = 0
  LastAngle = 0
  MakeFace = true
  Placement = pos=(-276.591,-28.0979,0) rot=(0,0,1;2.27137rad)
  Radius = 0.6
FEATURE [Part::Part2DObjectPython] Rectangle132  # Draft 2D object (typed FeaturePython)
  Area = 0
  ChamferSize = 0
  Columns = 1
  FilletRadius = 0
  Height = 6
  Length = 6
  MakeFace = false
  Placement = pos=(-267.868,-46.1855,0) rot=(0,0,1;2.34782rad)
  Rows = 1
FEATURE [Part::Part2DObjectPython] Circle132  # Draft 2D object (typed FeaturePython)
  Area = 1.13097
  FirstAngle = 0
  LastAngle = 0
  MakeFace = true
  Placement = pos=(-274.634,-43.5832,0) rot=(0,0,1;2.34782rad)
  Radius = 0.6
FEATURE [Part::Part2DObjectPython] Rectangle133  # Draft 2D object (typed FeaturePython)
  Area = 0
  ChamferSize = 0
  Columns = 1
  FilletRadius = 0
  Height = 6
  Length = 6
  MakeFace = false
  Placement = pos=(-254.488,-96.0552,0) rot=(0,0,1;2.3644rad)
  Rows = 1
FEATURE [App::FeaturePython] Text038  # WARN: FeaturePython — macro-defined, semantics opaque (R4)
  Placement = pos=(-261.188,-89.1931,0) rot=(0,0,-1;1.07373rad)
  Text = 0
FEATURE [App::FeaturePython] Text039  # WARN: FeaturePython — macro-defined, semantics opaque (R4)
  Placement = pos=(-207.363,-176.926,0) rot=(0,0,-1;6.27708rad)
  Text = 1
FEATURE [Part::Part2DObjectPython] Circle133  # Draft 2D object (typed FeaturePython)
  Area = 1.13097
  FirstAngle = 0
  LastAngle = 0
  MakeFace = true
  Placement = pos=(-261.296,-93.5654,0) rot=(0,0,1;2.3644rad)
  Radius = 0.6
FEATURE [Part::Part2DObjectPython] Rectangle134  # Draft 2D object (typed FeaturePython)
  Area = 0
  ChamferSize = 0
  Columns = 1
  FilletRadius = 0
  Height = 6
  Length = 6
  MakeFace = false
  Placement = pos=(-248.708,-110.376,0) rot=(0,0,1;2.36667rad)
  Rows = 1
FEATURE [Part::Part2DObjectPython] Circle134  # Draft 2D object (typed FeaturePython)
  Area = 1.13097
  FirstAngle = 0
  LastAngle = 0
  MakeFace = true
  Placement = pos=(-255.522,-107.901,0) rot=(0,0,1;2.36667rad)
  Radius = 0.6
FEATURE [Part::Part2DObjectPython] Rectangle135  # Draft 2D object (typed FeaturePython)
  Area = 0
  ChamferSize = 0
  Columns = 1
  FilletRadius = 0
  Height = 6
  Length = 6
  MakeFace = false
  Placement = pos=(-242.157,-123.907,0) rot=(0,0,1;2.47505rad)
  Rows = 1
FEATURE [Part::Part2DObjectPython] Circle135  # Draft 2D object (typed FeaturePython)
  Area = 1.13097
  FirstAngle = 0
  LastAngle = 0
  MakeFace = true
  Placement = pos=(-249.199,-122.184,0) rot=(0,0,1;2.47505rad)
  Radius = 0.6
FEATURE [Part::Part2DObjectPython] Rectangle136  # Draft 2D object (typed FeaturePython)
  Area = 0
  ChamferSize = 0
  Columns = 1
  FilletRadius = 0
  Height = 6
  Length = 6
  MakeFace = false
  Placement = pos=(-236.995,-134.272,0) rot=(0,0,1;3.4294rad)
  Rows = 1
FEATURE [Part::Part2DObjectPython] Circle136  # Draft 2D object (typed FeaturePython)
  Area = 1.13097
  FirstAngle = 0
  LastAngle = 0
  MakeFace = true
  Placement = pos=(-242.472,-139.022,0) rot=(0,0,1;3.4294rad)
  Radius = 0.6
FEATURE [Part::Part2DObjectPython] Rectangle137  # Draft 2D object (typed FeaturePython)
  Area = 0
  ChamferSize = 0
  Columns = 1
  FilletRadius = 0
  Height = 6
  Length = 6
  MakeFace = false
  Placement = pos=(-234.842,-149.541,0) rot=(0,0,1;5.10631rad)
  Rows = 1
FEATURE [Part::Part2DObjectPython] Circle137  # Draft 2D object (typed FeaturePython)
  Area = 1.13097
  FirstAngle = 0
  LastAngle = 0
  MakeFace = true
  Placement = pos=(-229.538,-154.484,0) rot=(0,0,1;5.10631rad)
  Radius = 0.6
FEATURE [Part::Part2DObjectPython] Rectangle138  # Draft 2D object (typed FeaturePython)
  Area = 0
  ChamferSize = 0
  Columns = 1
  FilletRadius = 0
  Height = 6
  Length = 6
  MakeFace = false
  Placement = pos=(-226.312,-163.338,0) rot=(0,0,1;5.37684rad)
  Rows = 1
FEATURE [Part::Part2DObjectPython] Circle138  # Draft 2D object (typed FeaturePython)
  Area = 1.13097
  FirstAngle = 0
  LastAngle = 0
  MakeFace = true
  Placement = pos=(-219.88,-166.684,0) rot=(0,0,1;5.37684rad)
  Radius = 0.6
FEATURE [Part::Part2DObjectPython] Rectangle139  # Draft 2D object (typed FeaturePython)
  Area = 0
  ChamferSize = 0
  Columns = 1
  FilletRadius = 0
  Height = 6
  Length = 6
  MakeFace = false
  Placement = pos=(-215.58,-179.02,0) rot=(0,0,1;0rad)
  Rows = 1
FEATURE [Part::Part2DObjectPython] Circle139  # Draft 2D object (typed FeaturePython)
  Area = 1.13097
  FirstAngle = 0
  LastAngle = 0
  MakeFace = true
  Placement = pos=(-208.98,-176.02,0) rot=(0,0,1;0rad)
  Radius = 0.6
FEATURE [Part::Part2DObjectPython] Rectangle140  # Draft 2D object (typed FeaturePython)
  Area = 0
  ChamferSize = 0
  Columns = 1
  FilletRadius = 0
  Height = 6
  Length = 6
  MakeFace = false
  Placement = pos=(-179.02,-215.58,0) rot=(0,0,1;0rad)
  Rows = 1
FEATURE [App::FeaturePython] Text040  # WARN: FeaturePython — macro-defined, semantics opaque (R4)
  Placement = pos=(-181.597,-207.836,0) rot=(0,0,-1;0.550128rad)
  Text = 0
FEATURE [App::FeaturePython] Text041  # WARN: FeaturePython — macro-defined, semantics opaque (R4)
  Placement = pos=(-91.1209,-256.902,0) rot=(0,0,-1;5.75348rad)
  Text = 2
FEATURE [Part::Part2DObjectPython] Circle140  # Draft 2D object (typed FeaturePython)
  Area = 1.13097
  FirstAngle = 0
  LastAngle = 0
  MakeFace = true
  Placement = pos=(-172.42,-212.58,0) rot=(0,0,1;0rad)
  Radius = 0.6
FEATURE [Part::Part2DObjectPython] Rectangle141  # Draft 2D object (typed FeaturePython)
  Area = 0
  ChamferSize = 0
  Columns = 1
  FilletRadius = 0
  Height = 6
  Length = 6
  MakeFace = false
  Placement = pos=(-166.85,-225.1,0) rot=(0,0,1;0rad)
  Rows = 1
FEATURE [Part::Part2DObjectPython] Circle141  # Draft 2D object (typed FeaturePython)
  Area = 1.13097
  FirstAngle = 0
  LastAngle = 0
  MakeFace = true
  Placement = pos=(-160.25,-222.1,0) rot=(0,0,1;0rad)
  Radius = 0.6
FEATURE [Part::Part2DObjectPython] Rectangle142  # Draft 2D object (typed FeaturePython)
  Area = 0
  ChamferSize = 0
  Columns = 1
  FilletRadius = 0
  Height = 6
  Length = 6
  MakeFace = false
  Placement = pos=(-153.769,-234.266,0) rot=(0,0,1;0.12322rad)
  Rows = 1
FEATURE [Part::Part2DObjectPython] Circle142  # Draft 2D object (typed FeaturePython)
  Area = 1.13097
  FirstAngle = 0
  LastAngle = 0
  MakeFace = true
  Placement = pos=(-147.587,-230.478,0) rot=(0,0,1;0.12322rad)
  Radius = 0.6
FEATURE [Part::Part2DObjectPython] Rectangle143  # Draft 2D object (typed FeaturePython)
  Area = 0
  ChamferSize = 0
  Columns = 1
  FilletRadius = 0
  Height = 6
  Length = 6
  MakeFace = false
  Placement = pos=(-140.067,-242.725,0) rot=(0,0,1;0.27646rad)
  Rows = 1
FEATURE [Part::Part2DObjectPython] Circle143  # Draft 2D object (typed FeaturePython)
  Area = 1.13097
  FirstAngle = 0
  LastAngle = 0
  MakeFace = true
  Placement = pos=(-134.537,-238.037,0) rot=(0,0,1;0.27646rad)
  Radius = 0.6
FEATURE [Part::Part2DObjectPython] Rectangle144  # Draft 2D object (typed FeaturePython)
  Area = 0
  ChamferSize = 0
  Columns = 1
  FilletRadius = 0
  Height = 6
  Length = 6
  MakeFace = false
  Placement = pos=(-125.897,-250.343,0) rot=(0,0,1;0.427257rad)
  Rows = 1
FEATURE [Part::Part2DObjectPython] Circle144  # Draft 2D object (typed FeaturePython)
  Area = 1.13097
  FirstAngle = 0
  LastAngle = 0
  MakeFace = true
  Placement = pos=(-121.134,-244.878,0) rot=(0,0,1;0.427257rad)
  Radius = 0.6
FEATURE [Part::Part2DObjectPython] Rectangle145  # Draft 2D object (typed FeaturePython)
  Area = 0
  ChamferSize = 0
  Columns = 1
  FilletRadius = 0
  Height = 6
  Length = 6
  MakeFace = false
  Placement = pos=(-111.303,-257.1,0) rot=(0,0,1;0.575784rad)
  Rows = 1
FEATURE [Part::Part2DObjectPython] Circle145  # Draft 2D object (typed FeaturePython)
  Area = 1.13097
  FirstAngle = 0
  LastAngle = 0
  MakeFace = true
  Placement = pos=(-107.4,-250.99,0) rot=(0,0,1;0.575784rad)
  Radius = 0.6
FEATURE [Part::Part2DObjectPython] Rectangle146  # Draft 2D object (typed FeaturePython)
  Area = 0
  ChamferSize = 0
  Columns = 1
  FilletRadius = 0
  Height = 6
  Length = 6
  MakeFace = false
  Placement = pos=(-96.3571,-262.964,0) rot=(0,0,1;0.722392rad)
  Rows = 1
FEATURE [Part::Part2DObjectPython] Circle146  # Draft 2D object (typed FeaturePython)
  Area = 1.13097
  FirstAngle = 0
  LastAngle = 0
  MakeFace = true
  Placement = pos=(-93.3892,-256.35,0) rot=(0,0,1;0.722392rad)
  Radius = 0.6
FEATURE [Part::Part2DObjectPython] Rectangle147  # Draft 2D object (typed FeaturePython)
  Area = 0
  ChamferSize = 0
  Columns = 1
  FilletRadius = 0
  Height = 6
  Length = 6
  MakeFace = false
  Placement = pos=(-44.4122,-275.98,0) rot=(0,0,1;1.20742rad)
  Rows = 1
FEATURE [App::FeaturePython] Text042  # WARN: FeaturePython — macro-defined, semantics opaque (R4)
  Placement = pos=(-53.3517,-270.79,0) rot=(0,0,1;6.25666rad)
  Text = 0
FEATURE [App::FeaturePython] Text043  # WARN: FeaturePython — macro-defined, semantics opaque (R4)
  Placement = pos=(49.5386,-268.047,0) rot=(0,0,1;1.05331rad)
  Text = 3
FEATURE [Part::Part2DObjectPython] Circle147  # Draft 2D object (typed FeaturePython)
  Area = 1.13097
  FirstAngle = 0
  LastAngle = 0
  MakeFace = true
  Placement = pos=(-44.8704,-268.745,0) rot=(0,0,1;1.20742rad)
  Radius = 0.6
FEATURE [Part::Part2DObjectPython] Rectangle148  # Draft 2D object (typed FeaturePython)
  Area = 0
  ChamferSize = 0
  Columns = 1
  FilletRadius = 0
  Height = 6
  Length = 6
  MakeFace = false
  Placement = pos=(-28.5729,-277.85,0) rot=(0,0,1;1.35193rad)
  Rows = 1
FEATURE [Part::Part2DObjectPython] Circle148  # Draft 2D object (typed FeaturePython)
  Area = 1.13097
  FirstAngle = 0
  LastAngle = 0
  MakeFace = true
  Placement = pos=(-30.0684,-270.756,0) rot=(0,0,1;1.35193rad)
  Radius = 0.6
FEATURE [Part::Part2DObjectPython] Rectangle149  # Draft 2D object (typed FeaturePython)
  Area = 0
  ChamferSize = 0
  Columns = 1
  FilletRadius = 0
  Height = 6
  Length = 6
  MakeFace = false
  Placement = pos=(-18.45,-278.57,0) rot=(0,0,1;0rad)
  Rows = 1
FEATURE [Part::Part2DObjectPython] Circle149  # Draft 2D object (typed FeaturePython)
  Area = 1.13097
  FirstAngle = 0
  LastAngle = 0
  MakeFace = true
  Placement = pos=(-11.85,-275.57,0) rot=(0,0,1;0rad)
  Radius = 0.6
FEATURE [Part::Part2DObjectPython] Rectangle150  # Draft 2D object (typed FeaturePython)
  Area = 0
  ChamferSize = 0
  Columns = 1
  FilletRadius = 0
  Height = 6
  Length = 6
  MakeFace = false
  Placement = pos=(-3,-279,0) rot=(0,0,1;0rad)
  Rows = 1
FEATURE [Part::Part2DObjectPython] Circle150  # Draft 2D object (typed FeaturePython)
  Area = 1.13097
  FirstAngle = 0
  LastAngle = 0
  MakeFace = true
  Placement = pos=(3.6,-276,0) rot=(0,0,1;0rad)
  Radius = 0.6
FEATURE [Part::Part2DObjectPython] Rectangle151  # Draft 2D object (typed FeaturePython)
  Area = 0
  ChamferSize = 0
  Columns = 1
  FilletRadius = 0
  Height = 6
  Length = 6
  MakeFace = false
  Placement = pos=(19.0302,-277.846,0) rot=(0,0,1;1.78984rad)
  Rows = 1
FEATURE [Part::Part2DObjectPython] Circle151  # Draft 2D object (typed FeaturePython)
  Area = 1.13097
  FirstAngle = 0
  LastAngle = 0
  MakeFace = true
  Placement = pos=(14.6678,-272.056,0) rot=(0,0,1;1.78984rad)
  Radius = 0.6
FEATURE [Part::Part2DObjectPython] Rectangle152  # Draft 2D object (typed FeaturePython)
  Area = 0
  ChamferSize = 0
  Columns = 1
  FilletRadius = 0
  Height = 6
  Length = 6
  MakeFace = false
  Placement = pos=(34.7267,-275.994,0) rot=(0,0,1;1.93784rad)
  Rows = 1
FEATURE [Part::Part2DObjectPython] Circle152  # Draft 2D object (typed FeaturePython)
  Area = 1.13097
  FirstAngle = 0
  LastAngle = 0
  MakeFace = true
  Placement = pos=(29.5581,-270.91,0) rot=(0,0,1;1.93784rad)
  Radius = 0.6
FEATURE [Part::Part2DObjectPython] Rectangle153  # Draft 2D object (typed FeaturePython)
  Area = 0
  ChamferSize = 0
  Columns = 1
  FilletRadius = 0
  Height = 6
  Length = 6
  MakeFace = false
  Placement = pos=(50.2399,-273.238,0) rot=(0,0,1;2.08706rad)
  Rows = 1
FEATURE [Part::Part2DObjectPython] Circle153  # Draft 2D object (typed FeaturePython)
  Area = 1.13097
  FirstAngle = 0
  LastAngle = 0
  MakeFace = true
  Placement = pos=(44.3729,-268.979,0) rot=(0,0,1;2.08706rad)
  Radius = 0.6
FEATURE [Part::Part2DObjectPython] Rectangle154  # Draft 2D object (typed FeaturePython)
  Area = 0
  ChamferSize = 0
  Columns = 1
  FilletRadius = 0
  Height = 6
  Length = 6
  MakeFace = false
  Placement = pos=(100.208,-257.711,0) rot=(0,0,1;2.59879rad)
  Rows = 1
FEATURE [App::FeaturePython] Text044  # WARN: FeaturePython — macro-defined, semantics opaque (R4)
  Placement = pos=(89.1931,-261.188,0) rot=(0,0,-1;5.78612rad)
  Text = 0
FEATURE [App::FeaturePython] Text045  # WARN: FeaturePython — macro-defined, semantics opaque (R4)
  Placement = pos=(176.926,-207.363,0) rot=(0,0,1;1.57691rad)
  Text = 4
FEATURE [Part::Part2DObjectPython] Circle154  # Draft 2D object (typed FeaturePython)
  Area = 1.13097
  FirstAngle = 0
  LastAngle = 0
  MakeFace = true
  Placement = pos=(93.0074,-256.87,0) rot=(0,0,1;2.59879rad)
  Radius = 0.6
FEATURE [Part::Part2DObjectPython] Rectangle155  # Draft 2D object (typed FeaturePython)
  Area = 0
  ChamferSize = 0
  Columns = 1
  FilletRadius = 0
  Height = 6
  Length = 6
  MakeFace = false
  Placement = pos=(114.328,-251.299,0) rot=(0,0,1;2.75588rad)
  Rows = 1
FEATURE [Part::Part2DObjectPython] Circle155  # Draft 2D object (typed FeaturePython)
  Area = 1.13097
  FirstAngle = 0
  LastAngle = 0
  MakeFace = true
  Placement = pos=(107.084,-251.596,0) rot=(0,0,1;2.75588rad)
  Radius = 0.6
FEATURE [Part::Part2DObjectPython] Rectangle156  # Draft 2D object (typed FeaturePython)
  Area = 0
  ChamferSize = 0
  Columns = 1
  FilletRadius = 0
  Height = 6
  Length = 6
  MakeFace = false
  Placement = pos=(128.008,-244.121,0) rot=(0,0,1;2.91487rad)
  Rows = 1
FEATURE [Part::Part2DObjectPython] Circle156  # Draft 2D object (typed FeaturePython)
  Area = 1.13097
  FirstAngle = 0
  LastAngle = 0
  MakeFace = true
  Placement = pos=(120.902,-245.561,0) rot=(0,0,1;2.91487rad)
  Radius = 0.6
FEATURE [Part::Part2DObjectPython] Rectangle157  # Draft 2D object (typed FeaturePython)
  Area = 0
  ChamferSize = 0
  Columns = 1
  FilletRadius = 0
  Height = 6
  Length = 6
  MakeFace = false
  Placement = pos=(141.191,-236.224,0) rot=(0,0,1;3.07562rad)
  Rows = 1
FEATURE [Part::Part2DObjectPython] Circle157  # Draft 2D object (typed FeaturePython)
  Area = 1.13097
  FirstAngle = 0
  LastAngle = 0
  MakeFace = true
  Placement = pos=(134.408,-238.783,0) rot=(0,0,1;3.07562rad)
  Radius = 0.6
FEATURE [Part::Part2DObjectPython] Rectangle158  # Draft 2D object (typed FeaturePython)
  Area = 0
  ChamferSize = 0
  Columns = 1
  FilletRadius = 0
  Height = 6
  Length = 6
  MakeFace = false
  Placement = pos=(153.861,-227.648,0) rot=(0,0,1;3.23689rad)
  Rows = 1
FEATURE [Part::Part2DObjectPython] Circle158  # Draft 2D object (typed FeaturePython)
  Area = 1.13097
  FirstAngle = 0
  LastAngle = 0
  MakeFace = true
  Placement = pos=(147.576,-231.263,0) rot=(0,0,1;3.23689rad)
  Radius = 0.6
FEATURE [Part::Part2DObjectPython] Rectangle159  # Draft 2D object (typed FeaturePython)
  Area = 0
  ChamferSize = 0
  Columns = 1
  FilletRadius = 0
  Height = 6
  Length = 6
  MakeFace = false
  Placement = pos=(165.995,-218.44,0) rot=(0,0,1;3.39693rad)
  Rows = 1
FEATURE [Part::Part2DObjectPython] Circle159  # Draft 2D object (typed FeaturePython)
  Area = 1.13097
  FirstAngle = 0
  LastAngle = 0
  MakeFace = true
  Placement = pos=(160.367,-223.009,0) rot=(0,0,1;3.39693rad)
  Radius = 0.6
FEATURE [Part::Part2DObjectPython] Rectangle160  # Draft 2D object (typed FeaturePython)
  Area = 0
  ChamferSize = 0
  Columns = 1
  FilletRadius = 0
  Height = 6
  Length = 6
  MakeFace = false
  Placement = pos=(177.574,-208.632,0) rot=(0,0,1;3.55209rad)
  Rows = 1
FEATURE [Part::Part2DObjectPython] Circle160  # Draft 2D object (typed FeaturePython)
  Area = 1.13097
  FirstAngle = 0
  LastAngle = 0
  MakeFace = true
  Placement = pos=(172.719,-214.017,0) rot=(0,0,1;3.55209rad)
  Radius = 0.6
FEATURE [Part::Part2DObjectPython] Rectangle161  # Draft 2D object (typed FeaturePython)
  Area = 0
  ChamferSize = 0
  Columns = 1
  FilletRadius = 0
  Height = 6
  Length = 6
  MakeFace = false
  Placement = pos=(212.493,-171.778,0) rot=(0,0,1;3.94741rad)
  Rows = 1
FEATURE [App::FeaturePython] Text046  # WARN: FeaturePython — macro-defined, semantics opaque (R4)
  Placement = pos=(207.836,-181.597,0) rot=(0,0,-1;5.26252rad)
  Text = 0
FEATURE [App::FeaturePython] Text047  # WARN: FeaturePython — macro-defined, semantics opaque (R4)
  Placement = pos=(256.902,-91.1209,0) rot=(0,0,1;2.1005rad)
  Text = 5
FEATURE [Part::Part2DObjectPython] Circle161  # Draft 2D object (typed FeaturePython)
  Area = 1.13097
  FirstAngle = 0
  LastAngle = 0
  MakeFace = true
  Placement = pos=(210.087,-178.617,0) rot=(0,0,1;3.94741rad)
  Radius = 0.6
FEATURE [Part::Part2DObjectPython] Rectangle162  # Draft 2D object (typed FeaturePython)
  Area = 0
  ChamferSize = 0
  Columns = 1
  FilletRadius = 0
  Height = 6
  Length = 6
  MakeFace = false
  Placement = pos=(222.439,-159.621,0) rot=(0,0,1;3.84706rad)
  Rows = 1
FEATURE [Part::Part2DObjectPython] Circle162  # Draft 2D object (typed FeaturePython)
  Area = 1.13097
  FirstAngle = 0
  LastAngle = 0
  MakeFace = true
  Placement = pos=(219.359,-166.184,0) rot=(0,0,1;3.84706rad)
  Radius = 0.6
FEATURE [Part::Part2DObjectPython] Rectangle163  # Draft 2D object (typed FeaturePython)
  Area = 0
  ChamferSize = 0
  Columns = 1
  FilletRadius = 0
  Height = 6
  Length = 6
  MakeFace = false
  Placement = pos=(234.1,-153.968,0) rot=(0,0,1;1.63293rad)
  Rows = 1
FEATURE [Part::Part2DObjectPython] Circle163  # Draft 2D object (typed FeaturePython)
  Area = 1.13097
  FirstAngle = 0
  LastAngle = 0
  MakeFace = true
  Placement = pos=(230.696,-147.567,0) rot=(0,0,1;1.63293rad)
  Radius = 0.6
FEATURE [Part::Part2DObjectPython] Rectangle164  # Draft 2D object (typed FeaturePython)
  Area = 0
  ChamferSize = 0
  Columns = 1
  FilletRadius = 0
  Height = 6
  Length = 6
  MakeFace = false
  Placement = pos=(241.489,-141.45,0) rot=(0,0,1;1.40656rad)
  Rows = 1
FEATURE [Part::Part2DObjectPython] Circle164  # Draft 2D object (typed FeaturePython)
  Area = 1.13097
  FirstAngle = 0
  LastAngle = 0
  MakeFace = true
  Placement = pos=(239.609,-134.448,0) rot=(0,0,1;1.40656rad)
  Radius = 0.6
FEATURE [Part::Part2DObjectPython] Rectangle165  # Draft 2D object (typed FeaturePython)
  Area = 0
  ChamferSize = 0
  Columns = 1
  FilletRadius = 0
  Height = 6
  Length = 6
  MakeFace = false
  Placement = pos=(248.917,-127.803,0) rot=(0,0,1;1.42942rad)
  Rows = 1
FEATURE [Part::Part2DObjectPython] Circle165  # Draft 2D object (typed FeaturePython)
  Area = 1.13097
  FirstAngle = 0
  LastAngle = 0
  MakeFace = true
  Placement = pos=(246.877,-120.846,0) rot=(0,0,1;1.42942rad)
  Radius = 0.6
FEATURE [Part::Part2DObjectPython] Rectangle166  # Draft 2D object (typed FeaturePython)
  Area = 0
  ChamferSize = 0
  Columns = 1
  FilletRadius = 0
  Height = 6
  Length = 6
  MakeFace = false
  Placement = pos=(255.671,-113.675,0) rot=(0,0,1;1.48161rad)
  Rows = 1
FEATURE [Part::Part2DObjectPython] Circle166  # Draft 2D object (typed FeaturePython)
  Area = 1.13097
  FirstAngle = 0
  LastAngle = 0
  MakeFace = true
  Placement = pos=(253.271,-106.834,0) rot=(0,0,1;1.48161rad)
  Radius = 0.6
FEATURE [Part::Part2DObjectPython] Rectangle167  # Draft 2D object (typed FeaturePython)
  Area = 0
  ChamferSize = 0
  Columns = 1
  FilletRadius = 0
  Height = 6
  Length = 6
  MakeFace = false
  Placement = pos=(261.639,-99.1787,0) rot=(0,0,1;1.54078rad)
  Rows = 1
FEATURE [Part::Part2DObjectPython] Circle167  # Draft 2D object (typed FeaturePython)
  Area = 1.13097
  FirstAngle = 0
  LastAngle = 0
  MakeFace = true
  Placement = pos=(258.838,-92.4916,0) rot=(0,0,1;1.54078rad)
  Radius = 0.6
FEATURE [App::DocumentObjectGroup] Everything001
  Group = -> [Rectangle084,Circle084,Rectangle085,Circle085,Rectangle086,Circle086,Rectangle087,Circle087,Rectangle088,Circle088,Rectangle089,Circle089,Rectangle090,Circle090,Rectangle091,Circle091,Rectangle092,Circle092,Rectangle093,Circle093,Rectangle094,Circle094,Rectangle095,Circle095,Rectangle096,Circle096,Rectangle097,Circle097,Rectangle098,Circle098,Rectangle099,Circle099,Rectangle100,Circle100,+134 more]
